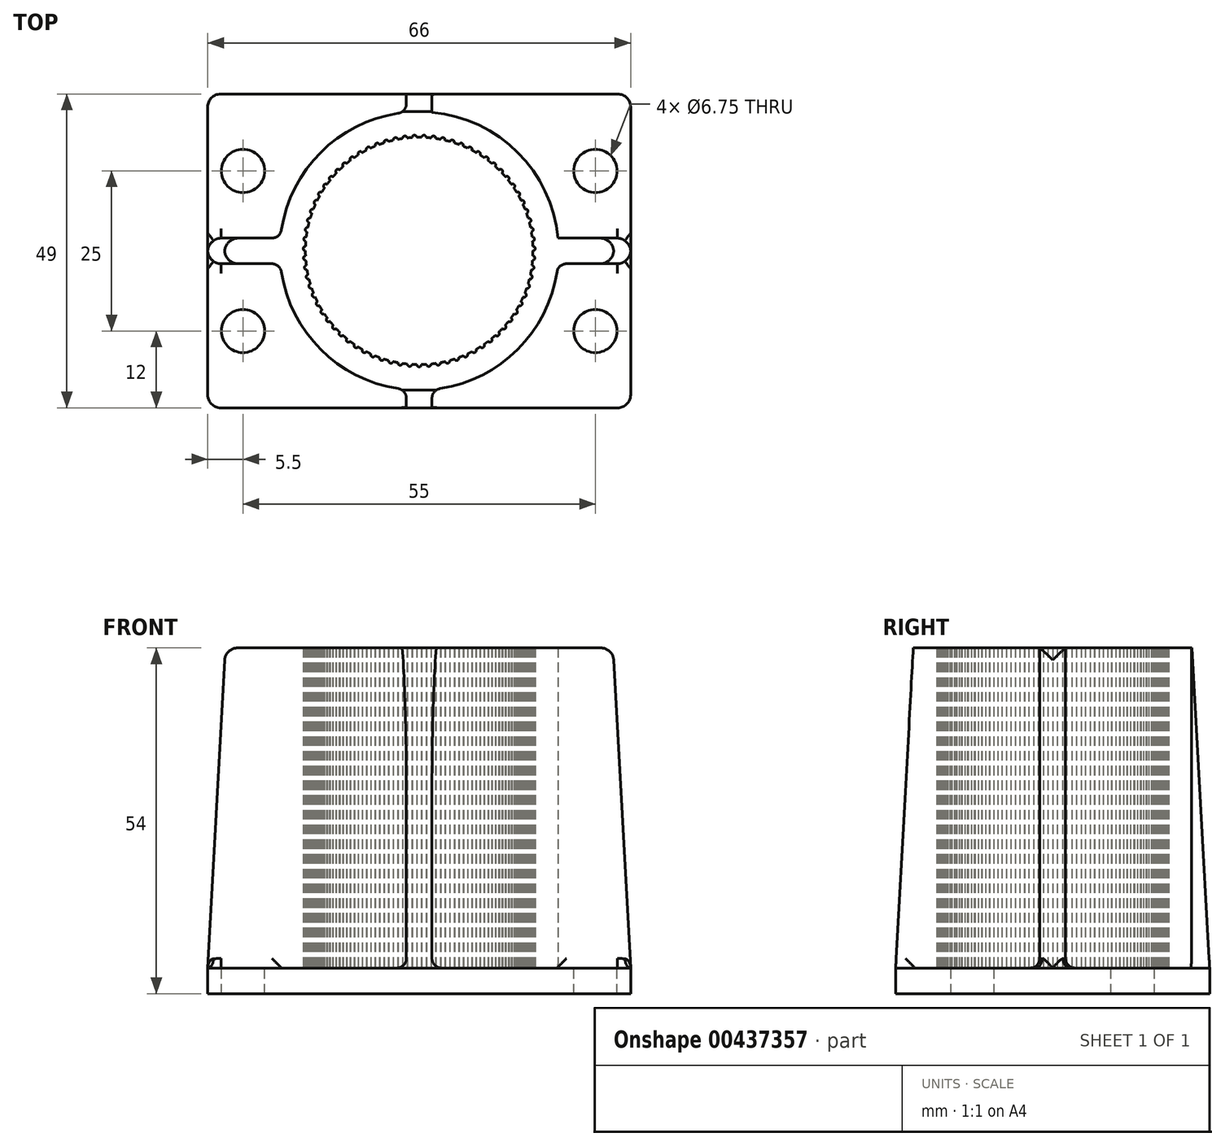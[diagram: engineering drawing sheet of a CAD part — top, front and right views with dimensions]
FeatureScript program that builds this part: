
annotation { "Feature Type Name" : "Feature", "Feature Type Description" : "" }
export const myFeature = defineFeature(function(context is Context, id is Id, definition is map)
    precondition{}
    {
        {
            assignVariable(context, id + "F0", {"name" : "PrintingOffset", "anyValue" : .5});
        }
        {
            assignVariable(context, id + "F1", {"name" : "BoltHoleDiameter", "anyValue" : 6.25 + getVariable(context, 'PrintingOffset')});
        }
        {
            assignVariable(context, id + "F2", {"name" : "PlateWidth", "anyValue" : 49});
        }
        {
            assignVariable(context, id + "F3", {"name" : "TableLegDiameter", "anyValue" : 35 + getVariable(context, 'PrintingOffset')});
        }
        {
            assignVariable(context, id + "F4", {"name" : "WallThickness", "anyValue" : 4});
        }
        {
            var Q0;
            Q0=qCreatedBy(makeId("Top.planeOp"),FACE);
            var sketch = newSketch(context, id + "F5", { "sketchPlane" : qUnion([Q0])});
            skLineSegment(sketch, "E0.rect.bottom", {"start": v(33, 24.5) * mm, "end": v(-33, 24.5) * mm});
            skLineSegment(sketch, "E0.rect.top", {"start": v(33, -24.5) * mm, "end": v(-33, -24.5) * mm});
            skLineSegment(sketch, "E0.rect.left", {"start": v(33, 24.5) * mm, "end": v(33, -24.5) * mm});
            skLineSegment(sketch, "E0.rect.right", {"start": v(-33, 24.5) * mm, "end": v(-33, -24.5) * mm});
            skPoint(sketch, "E0.rect.middle", {"position": v(0, 0) * mm});
            skCircle(sketch, "E1", {"center": v(0, 0) * mm, "radius": 17.75 * mm});
            skLineSegment(sketch, "E2", {"start": v(0, 24.5) * mm, "end": v(0, -24.5) * mm, "construction": true});
            skLineSegment(sketch, "E3", {"start": v(-33, 0) * mm, "end": v(33, 0) * mm, "construction": true});
            skCircle(sketch, "E4.0", {"center": v(0, 0) * mm, "radius": 21.75 * mm});
            skLineSegment(sketch, "E5.3.0", {"start": v(-21.66, 2) * mm, "end": v(-33, 2) * mm});
            skLineSegment(sketch, "E5.3.1", {"start": v(-21.66, -2) * mm, "end": v(-33, -2) * mm});
            skPoint(sketch, "E6", {"position": v(-27.5, 12.5) * mm});
            skArc(sketch, "E7", {"start": v(-0.35, -17.75) * mm, "mid": v(0, -18.1) * mm, "end": v(0.35, -17.75) * mm});
            skArc(sketch, "E8.1.0", {"start": v(1.14, -17.71) * mm, "mid": v(1.51, -18.04) * mm, "end": v(1.83, -17.66) * mm});
            skArc(sketch, "E8.2.0", {"start": v(2.61, -17.56) * mm, "mid": v(3.02, -17.85) * mm, "end": v(3.3, -17.44) * mm});
            skArc(sketch, "E8.3.0", {"start": v(4.07, -17.28) * mm, "mid": v(4.5, -17.53) * mm, "end": v(4.75, -17.1) * mm});
            skArc(sketch, "E8.4.0", {"start": v(5.5, -16.87) * mm, "mid": v(5.95, -17.1) * mm, "end": v(6.17, -16.64) * mm});
            skArc(sketch, "E8.5.0", {"start": v(6.9, -16.35) * mm, "mid": v(7.36, -16.54) * mm, "end": v(7.54, -16.07) * mm});
            skArc(sketch, "E8.6.0", {"start": v(8.24, -15.72) * mm, "mid": v(8.72, -15.86) * mm, "end": v(8.86, -15.38) * mm});
            skArc(sketch, "E8.7.0", {"start": v(9.53, -14.98) * mm, "mid": v(10.02, -15.08) * mm, "end": v(10.11, -14.59) * mm});
            skArc(sketch, "E8.8.0", {"start": v(10.75, -14.13) * mm, "mid": v(11.24, -14.18) * mm, "end": v(11.3, -13.7) * mm});
            skArc(sketch, "E8.9.0", {"start": v(11.9, -13.18) * mm, "mid": v(12.4, -13.2) * mm, "end": v(12.4, -12.7) * mm});
            skArc(sketch, "E8.10.0", {"start": v(12.95, -12.13) * mm, "mid": v(13.45, -12.11) * mm, "end": v(13.42, -11.61) * mm});
            skArc(sketch, "E8.11.0", {"start": v(13.92, -11) * mm, "mid": v(14.42, -10.94) * mm, "end": v(14.35, -10.45) * mm});
            skArc(sketch, "E8.12.0", {"start": v(14.8, -9.8) * mm, "mid": v(15.28, -9.7) * mm, "end": v(15.17, -9.21) * mm});
            skArc(sketch, "E8.13.0", {"start": v(15.56, -8.53) * mm, "mid": v(16.04, -8.39) * mm, "end": v(15.89, -7.91) * mm});
            skArc(sketch, "E8.14.0", {"start": v(16.22, -7.2) * mm, "mid": v(16.69, -7.01) * mm, "end": v(16.5, -6.55) * mm});
            skArc(sketch, "E8.15.0", {"start": v(16.77, -5.82) * mm, "mid": v(17.21, -5.6) * mm, "end": v(16.99, -5.15) * mm});
            skArc(sketch, "E8.16.0", {"start": v(17.2, -4.4) * mm, "mid": v(17.62, -4.13) * mm, "end": v(17.36, -3.71) * mm});
            skArc(sketch, "E8.17.0", {"start": v(17.5, -2.94) * mm, "mid": v(17.9, -2.64) * mm, "end": v(17.6, -2.25) * mm});
            skArc(sketch, "E8.18.0", {"start": v(17.69, -1.46) * mm, "mid": v(18.06, -1.14) * mm, "end": v(17.73, -0.77) * mm});
            skArc(sketch, "E8.19.0", {"start": v(17.75, 0.02) * mm, "mid": v(18.1, 0.38) * mm, "end": v(17.74, 0.72) * mm});
            skArc(sketch, "E8.20.0", {"start": v(17.69, 1.5) * mm, "mid": v(18, 1.9) * mm, "end": v(17.61, 2.2) * mm});
            skArc(sketch, "E8.21.0", {"start": v(17.5, 2.98) * mm, "mid": v(17.78, 3.4) * mm, "end": v(17.37, 3.67) * mm});
            skArc(sketch, "E8.22.0", {"start": v(17.19, 4.44) * mm, "mid": v(17.43, 4.87) * mm, "end": v(17, 5.1) * mm});
            skArc(sketch, "E8.23.0", {"start": v(16.76, 5.86) * mm, "mid": v(16.96, 6.3) * mm, "end": v(16.51, 6.51) * mm});
            skArc(sketch, "E8.24.0", {"start": v(16.2, 7.24) * mm, "mid": v(16.38, 7.7) * mm, "end": v(15.9, 7.87) * mm});
            skArc(sketch, "E8.25.0", {"start": v(15.54, 8.57) * mm, "mid": v(15.68, 9.05) * mm, "end": v(15.2, 9.18) * mm});
            skArc(sketch, "E8.26.0", {"start": v(14.77, 9.84) * mm, "mid": v(14.86, 10.33) * mm, "end": v(14.37, 10.42) * mm});
            skArc(sketch, "E8.27.0", {"start": v(13.9, 11.04) * mm, "mid": v(13.95, 11.54) * mm, "end": v(13.45, 11.58) * mm});
            skArc(sketch, "E8.28.0", {"start": v(12.92, 12.17) * mm, "mid": v(12.93, 12.66) * mm, "end": v(12.43, 12.67) * mm});
            skArc(sketch, "E8.29.0", {"start": v(11.86, 13.2) * mm, "mid": v(11.83, 13.7) * mm, "end": v(11.33, 13.66) * mm});
            skArc(sketch, "E8.30.0", {"start": v(10.71, 14.15) * mm, "mid": v(10.64, 14.64) * mm, "end": v(10.15, 14.56) * mm});
            skArc(sketch, "E8.31.0", {"start": v(9.5, 15) * mm, "mid": v(9.38, 15.48) * mm, "end": v(8.9, 15.36) * mm});
            skArc(sketch, "E8.32.0", {"start": v(8.2, 15.74) * mm, "mid": v(8.05, 16.21) * mm, "end": v(7.58, 16.05) * mm});
            skArc(sketch, "E8.33.0", {"start": v(6.86, 16.37) * mm, "mid": v(6.66, 16.83) * mm, "end": v(6.2, 16.63) * mm});
            skArc(sketch, "E8.34.0", {"start": v(5.46, 16.89) * mm, "mid": v(5.23, 17.33) * mm, "end": v(4.8, 17.1) * mm});
            skArc(sketch, "E8.35.0", {"start": v(4.03, 17.29) * mm, "mid": v(3.76, 17.7) * mm, "end": v(3.35, 17.43) * mm});
            skArc(sketch, "E8.36.0", {"start": v(2.57, 17.56) * mm, "mid": v(2.27, 17.96) * mm, "end": v(1.88, 17.65) * mm});
            skArc(sketch, "E8.37.0", {"start": v(1.1, 17.72) * mm, "mid": v(0.76, 18.08) * mm, "end": v(0.4, 17.75) * mm});
            skArc(sketch, "E8.38.0", {"start": v(-0.4, 17.75) * mm, "mid": v(-0.76, 18.08) * mm, "end": v(-1.1, 17.72) * mm});
            skArc(sketch, "E8.39.0", {"start": v(-1.88, 17.65) * mm, "mid": v(-2.27, 17.96) * mm, "end": v(-2.57, 17.56) * mm});
            skArc(sketch, "E8.40.0", {"start": v(-3.35, 17.43) * mm, "mid": v(-3.76, 17.7) * mm, "end": v(-4.03, 17.29) * mm});
            skArc(sketch, "E8.41.0", {"start": v(-4.8, 17.1) * mm, "mid": v(-5.23, 17.33) * mm, "end": v(-5.46, 16.89) * mm});
            skArc(sketch, "E8.42.0", {"start": v(-6.2, 16.63) * mm, "mid": v(-6.66, 16.83) * mm, "end": v(-6.86, 16.37) * mm});
            skArc(sketch, "E8.43.0", {"start": v(-7.58, 16.05) * mm, "mid": v(-8.05, 16.21) * mm, "end": v(-8.2, 15.74) * mm});
            skArc(sketch, "E8.44.0", {"start": v(-8.9, 15.36) * mm, "mid": v(-9.38, 15.48) * mm, "end": v(-9.5, 15) * mm});
            skArc(sketch, "E8.45.0", {"start": v(-10.15, 14.56) * mm, "mid": v(-10.64, 14.64) * mm, "end": v(-10.71, 14.15) * mm});
            skArc(sketch, "E8.46.0", {"start": v(-11.33, 13.66) * mm, "mid": v(-11.83, 13.7) * mm, "end": v(-11.86, 13.2) * mm});
            skArc(sketch, "E8.47.0", {"start": v(-12.43, 12.67) * mm, "mid": v(-12.93, 12.66) * mm, "end": v(-12.92, 12.17) * mm});
            skArc(sketch, "E8.48.0", {"start": v(-13.45, 11.58) * mm, "mid": v(-13.95, 11.54) * mm, "end": v(-13.9, 11.04) * mm});
            skArc(sketch, "E8.49.0", {"start": v(-14.37, 10.42) * mm, "mid": v(-14.86, 10.33) * mm, "end": v(-14.77, 9.84) * mm});
            skArc(sketch, "E8.50.0", {"start": v(-15.2, 9.18) * mm, "mid": v(-15.68, 9.05) * mm, "end": v(-15.54, 8.57) * mm});
            skArc(sketch, "E8.51.0", {"start": v(-15.9, 7.87) * mm, "mid": v(-16.38, 7.7) * mm, "end": v(-16.2, 7.24) * mm});
            skArc(sketch, "E8.52.0", {"start": v(-16.51, 6.51) * mm, "mid": v(-16.96, 6.3) * mm, "end": v(-16.76, 5.86) * mm});
            skArc(sketch, "E8.53.0", {"start": v(-17, 5.1) * mm, "mid": v(-17.43, 4.87) * mm, "end": v(-17.19, 4.44) * mm});
            skArc(sketch, "E8.54.0", {"start": v(-17.37, 3.67) * mm, "mid": v(-17.78, 3.4) * mm, "end": v(-17.5, 2.98) * mm});
            skArc(sketch, "E8.55.0", {"start": v(-17.61, 2.2) * mm, "mid": v(-18, 1.9) * mm, "end": v(-17.69, 1.5) * mm});
            skArc(sketch, "E8.56.0", {"start": v(-17.74, 0.72) * mm, "mid": v(-18.1, 0.38) * mm, "end": v(-17.75, 0.02) * mm});
            skArc(sketch, "E8.57.0", {"start": v(-17.73, -0.77) * mm, "mid": v(-18.06, -1.14) * mm, "end": v(-17.69, -1.46) * mm});
            skArc(sketch, "E8.58.0", {"start": v(-17.6, -2.25) * mm, "mid": v(-17.9, -2.64) * mm, "end": v(-17.5, -2.94) * mm});
            skArc(sketch, "E8.59.0", {"start": v(-17.36, -3.71) * mm, "mid": v(-17.62, -4.13) * mm, "end": v(-17.2, -4.4) * mm});
            skArc(sketch, "E8.60.0", {"start": v(-16.99, -5.15) * mm, "mid": v(-17.21, -5.6) * mm, "end": v(-16.77, -5.82) * mm});
            skArc(sketch, "E8.61.0", {"start": v(-16.5, -6.55) * mm, "mid": v(-16.69, -7.01) * mm, "end": v(-16.22, -7.2) * mm});
            skArc(sketch, "E8.62.0", {"start": v(-15.89, -7.91) * mm, "mid": v(-16.04, -8.39) * mm, "end": v(-15.56, -8.53) * mm});
            skArc(sketch, "E8.63.0", {"start": v(-15.17, -9.21) * mm, "mid": v(-15.28, -9.7) * mm, "end": v(-14.8, -9.8) * mm});
            skArc(sketch, "E8.64.0", {"start": v(-14.35, -10.45) * mm, "mid": v(-14.42, -10.94) * mm, "end": v(-13.92, -11) * mm});
            skArc(sketch, "E8.65.0", {"start": v(-13.42, -11.61) * mm, "mid": v(-13.45, -12.11) * mm, "end": v(-12.95, -12.13) * mm});
            skArc(sketch, "E8.66.0", {"start": v(-12.4, -12.7) * mm, "mid": v(-12.4, -13.2) * mm, "end": v(-11.9, -13.18) * mm});
            skArc(sketch, "E8.67.0", {"start": v(-11.3, -13.7) * mm, "mid": v(-11.24, -14.18) * mm, "end": v(-10.75, -14.13) * mm});
            skArc(sketch, "E8.68.0", {"start": v(-10.11, -14.59) * mm, "mid": v(-10.02, -15.08) * mm, "end": v(-9.53, -14.98) * mm});
            skArc(sketch, "E8.69.0", {"start": v(-8.86, -15.38) * mm, "mid": v(-8.72, -15.86) * mm, "end": v(-8.24, -15.72) * mm});
            skArc(sketch, "E9.2.70.0", {"start": v(-7.54, -16.07) * mm, "mid": v(-7.36, -16.54) * mm, "end": v(-6.9, -16.35) * mm});
            skArc(sketch, "E9.2.71.0", {"start": v(-6.17, -16.64) * mm, "mid": v(-5.95, -17.1) * mm, "end": v(-5.5, -16.87) * mm});
            skArc(sketch, "E9.2.72.0", {"start": v(-4.75, -17.1) * mm, "mid": v(-4.5, -17.53) * mm, "end": v(-4.07, -17.28) * mm});
            skArc(sketch, "E9.2.73.0", {"start": v(-3.3, -17.44) * mm, "mid": v(-3.02, -17.85) * mm, "end": v(-2.61, -17.56) * mm});
            skArc(sketch, "E9.2.74.0", {"start": v(-1.83, -17.66) * mm, "mid": v(-1.51, -18.04) * mm, "end": v(-1.14, -17.71) * mm});
            skLineSegment(sketch, "E10.MirrorCS", {"start": v(21.66, -2) * mm, "end": v(33, -2) * mm});
            skLineSegment(sketch, "E11.MirrorCS", {"start": v(21.66, 2) * mm, "end": v(33, 2) * mm});
            skLineSegment(sketch, "E12.MirrorCS", {"start": v(-2, 21.66) * mm, "end": v(-2, 24.5) * mm});
            skLineSegment(sketch, "E13.MirrorCS", {"start": v(2, 21.66) * mm, "end": v(2, 24.5) * mm});
            skLineSegment(sketch, "E14.MirrorCS", {"start": v(-2, -21.66) * mm, "end": v(-2, -24.5) * mm});
            skLineSegment(sketch, "E15.MirrorCS", {"start": v(2, -21.66) * mm, "end": v(2, -24.5) * mm});
            skPoint(sketch, "E16.MirrorP", {"position": v(-27.5, -12.5) * mm});
            skPoint(sketch, "E17.MirrorP", {"position": v(27.5, 12.5) * mm});
            skPoint(sketch, "E18.MirrorP", {"position": v(27.5, -12.5) * mm});
            skSolve(sketch);
        }
        {
            assignVariable(context, id + "F6", {"name" : "CylinderHeight", "anyValue" : 50});
        }
        {
            var Q0;
            Q0=makeQuery(id+"F5.imprint","IMPRINT",FACE,{"disambiguationData":[TD([[makeQuery(id+"F5.imprint","IMPRINT",EDGE,{"derivedFrom":sQuery(id+"F5.wireOp",EDGE,"E1")}),-1.0]])]});
            extrude(context, id + "F7", {"entities" : qUnion([Q0]), "depth" : (getVariable(context, 'CylinderHeight')) * mm});
        }
        {
            var Q0;
            {var subQ1=sQuery(id+"F5.wireOp",EDGE,"E5.3.0");Q0=makeQuery(id+"F5.imprint","IMPRINT",FACE,{"disambiguationData":[TD([[makeQuery(id+"F5.imprint","IMPRINT",EDGE,{"derivedFrom":subQ1}),1.0]])]});}
            var Q1;
            {var subQ2=sQuery(id+"F5.wireOp",EDGE,"E5.1.1");Q1=makeQuery(id+"F5.imprint","IMPRINT",FACE,{"disambiguationData":[TD([[makeQuery(id+"F5.imprint","IMPRINT",EDGE,{"derivedFrom":subQ2}),1.0]])]});}
            var Q2;
            {var subQ0=sQuery(id+"F5.wireOp",EDGE,"E1");var subQ1=sQuery(id+"F5.wireOp",EDGE,"E8.25.0");var subQ174=makeQuery(id+"F5.imprint","INTERSECT",VERTEX,{"disambiguationData":[OD(1.0)],"derivedFrom":[subQ0,subQ1]});Q2=makeQuery(id+"F5.imprint","IMPRINT",FACE,{"disambiguationData":[TD([[makeQuery(id+"F5.imprint","IMPRINT",EDGE,{"disambiguationData":[TD([[subQ174,-1.0]])],"derivedFrom":subQ0}),1.0]])]});}
            var Q3;
            {var subQ0=sQuery(id+"F5.wireOp",EDGE,"E5.1.0");Q3=makeQuery(id+"F5.imprint","IMPRINT",FACE,{"disambiguationData":[TD([[makeQuery(id+"F5.imprint","IMPRINT",EDGE,{"derivedFrom":subQ0}),1.0]])]});}
            var Q4;
            {var subQ86=sQuery(id+"F5.wireOp",EDGE,"E7");Q4=makeQuery(id+"F5.imprint","IMPRINT",FACE,{"disambiguationData":[TD([[makeQuery(id+"F5.imprint","IMPRINT",EDGE,{"derivedFrom":subQ86}),-1.0]])]});}
            var Q5;
            {var subQ1=sQuery(id+"F5.wireOp",EDGE,"E5.2.0");Q5=makeQuery(id+"F5.imprint","IMPRINT",FACE,{"disambiguationData":[TD([[makeQuery(id+"F5.imprint","IMPRINT",EDGE,{"derivedFrom":subQ1}),1.0]])]});}
            var Q6;
            {var subQ1=sQuery(id+"F5.wireOp",EDGE,"E5.2.1");Q6=makeQuery(id+"F5.imprint","IMPRINT",FACE,{"disambiguationData":[TD([[makeQuery(id+"F5.imprint","IMPRINT",EDGE,{"derivedFrom":subQ1}),1.0]])]});}
            var Q7;
            {var subQ0=sQuery(id+"F5.wireOp",EDGE,"108301c5-a481-47a9-95d8-fa25c03050fa");Q7=makeQuery(id+"F5.imprint","IMPRINT",FACE,{"disambiguationData":[TD([[makeQuery(id+"F5.imprint","IMPRINT",EDGE,{"derivedFrom":subQ0}),1.0]])]});}
            var Q8;
            {var subQ1=sQuery(id+"F5.wireOp",EDGE,"79e71fa4-d721-44c3-a3e5-dd1a67dfb6ba");Q8=makeQuery(id+"F5.imprint","IMPRINT",FACE,{"disambiguationData":[TD([[makeQuery(id+"F5.imprint","IMPRINT",EDGE,{"derivedFrom":subQ1}),1.0]])]});}
            var Q9;
            {var subQ1=sQuery(id+"F5.wireOp",EDGE,"79e71fa4-d721-44c3-a3e5-dd1a67dfb6ba");Q9=makeQuery(id+"F5.imprint","IMPRINT",FACE,{"disambiguationData":[TD([[makeQuery(id+"F5.imprint","IMPRINT",EDGE,{"derivedFrom":subQ1}),-1.0]])]});}
            var Q10;
            Q10=makeQuery(id+"F7.opExtrude","CAP_FACE",FACE,{"disambiguationData":[OSD([sQuery(id+"F5.wireOp",EDGE,"E1"),sQuery(id+"F5.wireOp",EDGE,"E4.0"),sQuery(id+"F5.wireOp",EDGE,"E7"),sQuery(id+"F5.wireOp",EDGE,"E8.1.0"),sQuery(id+"F5.wireOp",EDGE,"E8.2.0"),sQuery(id+"F5.wireOp",EDGE,"E8.3.0"),sQuery(id+"F5.wireOp",EDGE,"E8.4.0"),sQuery(id+"F5.wireOp",EDGE,"E8.5.0"),sQuery(id+"F5.wireOp",EDGE,"E8.6.0"),sQuery(id+"F5.wireOp",EDGE,"E8.7.0"),sQuery(id+"F5.wireOp",EDGE,"E8.8.0"),sQuery(id+"F5.wireOp",EDGE,"E8.9.0"),sQuery(id+"F5.wireOp",EDGE,"E8.10.0"),sQuery(id+"F5.wireOp",EDGE,"E8.11.0"),sQuery(id+"F5.wireOp",EDGE,"E8.12.0"),sQuery(id+"F5.wireOp",EDGE,"E8.13.0"),sQuery(id+"F5.wireOp",EDGE,"E8.14.0"),sQuery(id+"F5.wireOp",EDGE,"E8.15.0"),sQuery(id+"F5.wireOp",EDGE,"E8.16.0"),sQuery(id+"F5.wireOp",EDGE,"E8.17.0"),sQuery(id+"F5.wireOp",EDGE,"E8.18.0"),sQuery(id+"F5.wireOp",EDGE,"E8.19.0"),sQuery(id+"F5.wireOp",EDGE,"E8.20.0"),sQuery(id+"F5.wireOp",EDGE,"E8.21.0"),sQuery(id+"F5.wireOp",EDGE,"E8.22.0"),sQuery(id+"F5.wireOp",EDGE,"E8.23.0"),sQuery(id+"F5.wireOp",EDGE,"E8.24.0"),sQuery(id+"F5.wireOp",EDGE,"E8.25.0"),sQuery(id+"F5.wireOp",EDGE,"E8.26.0"),sQuery(id+"F5.wireOp",EDGE,"E8.27.0"),sQuery(id+"F5.wireOp",EDGE,"E8.28.0"),sQuery(id+"F5.wireOp",EDGE,"E8.29.0"),sQuery(id+"F5.wireOp",EDGE,"E8.30.0"),sQuery(id+"F5.wireOp",EDGE,"E8.31.0"),sQuery(id+"F5.wireOp",EDGE,"E8.32.0"),sQuery(id+"F5.wireOp",EDGE,"E8.33.0"),sQuery(id+"F5.wireOp",EDGE,"E8.34.0"),sQuery(id+"F5.wireOp",EDGE,"E8.35.0"),sQuery(id+"F5.wireOp",EDGE,"E8.36.0"),sQuery(id+"F5.wireOp",EDGE,"E8.37.0"),sQuery(id+"F5.wireOp",EDGE,"E8.38.0"),sQuery(id+"F5.wireOp",EDGE,"E8.39.0"),sQuery(id+"F5.wireOp",EDGE,"E8.40.0"),sQuery(id+"F5.wireOp",EDGE,"E8.41.0"),sQuery(id+"F5.wireOp",EDGE,"E8.42.0"),sQuery(id+"F5.wireOp",EDGE,"E8.43.0"),sQuery(id+"F5.wireOp",EDGE,"E8.44.0"),sQuery(id+"F5.wireOp",EDGE,"E8.45.0"),sQuery(id+"F5.wireOp",EDGE,"E8.46.0"),sQuery(id+"F5.wireOp",EDGE,"E8.47.0"),sQuery(id+"F5.wireOp",EDGE,"E8.48.0"),sQuery(id+"F5.wireOp",EDGE,"E8.49.0"),sQuery(id+"F5.wireOp",EDGE,"E8.50.0"),sQuery(id+"F5.wireOp",EDGE,"E8.51.0"),sQuery(id+"F5.wireOp",EDGE,"E8.52.0"),sQuery(id+"F5.wireOp",EDGE,"E8.53.0"),sQuery(id+"F5.wireOp",EDGE,"E8.54.0"),sQuery(id+"F5.wireOp",EDGE,"E8.55.0"),sQuery(id+"F5.wireOp",EDGE,"E8.56.0"),sQuery(id+"F5.wireOp",EDGE,"E8.57.0"),sQuery(id+"F5.wireOp",EDGE,"E8.58.0"),sQuery(id+"F5.wireOp",EDGE,"E8.59.0"),sQuery(id+"F5.wireOp",EDGE,"E8.60.0"),sQuery(id+"F5.wireOp",EDGE,"E8.61.0"),sQuery(id+"F5.wireOp",EDGE,"E8.62.0"),sQuery(id+"F5.wireOp",EDGE,"E8.63.0"),sQuery(id+"F5.wireOp",EDGE,"E8.64.0"),sQuery(id+"F5.wireOp",EDGE,"E8.65.0"),sQuery(id+"F5.wireOp",EDGE,"E8.66.0"),sQuery(id+"F5.wireOp",EDGE,"E8.67.0"),sQuery(id+"F5.wireOp",EDGE,"E8.68.0"),sQuery(id+"F5.wireOp",EDGE,"E8.69.0"),sQuery(id+"F5.wireOp",EDGE,"E8.70.0"),sQuery(id+"F5.wireOp",EDGE,"E8.71.0"),sQuery(id+"F5.wireOp",EDGE,"E8.72.0"),sQuery(id+"F5.wireOp",EDGE,"E8.73.0"),sQuery(id+"F5.wireOp",EDGE,"E8.74.0"),sQuery(id+"F5.wireOp",EDGE,"E8.75.0"),sQuery(id+"F5.wireOp",EDGE,"E8.76.0"),sQuery(id+"F5.wireOp",EDGE,"E8.77.0"),sQuery(id+"F5.wireOp",EDGE,"E8.78.0"),sQuery(id+"F5.wireOp",EDGE,"E8.79.0"),sQuery(id+"F5.wireOp",EDGE,"E8.80.0"),sQuery(id+"F5.wireOp",EDGE,"E8.81.0"),sQuery(id+"F5.wireOp",EDGE,"E8.82.0"),sQuery(id+"F5.wireOp",EDGE,"E8.83.0"),sQuery(id+"F5.wireOp",EDGE,"E8.84.0"),sQuery(id+"F5.wireOp",EDGE,"E8.85.0"),sQuery(id+"F5.wireOp",EDGE,"E8.86.0"),sQuery(id+"F5.wireOp",EDGE,"E8.87.0"),sQuery(id+"F5.wireOp",EDGE,"E8.88.0"),sQuery(id+"F5.wireOp",EDGE,"E8.89.0"),sQuery(id+"F5.wireOp",EDGE,"E8.90.0"),sQuery(id+"F5.wireOp",EDGE,"E8.91.0"),sQuery(id+"F5.wireOp",EDGE,"E8.92.0"),sQuery(id+"F5.wireOp",EDGE,"E8.93.0"),sQuery(id+"F5.wireOp",EDGE,"E8.94.0"),sQuery(id+"F5.wireOp",EDGE,"E8.95.0"),sQuery(id+"F5.wireOp",EDGE,"E8.96.0"),sQuery(id+"F5.wireOp",EDGE,"E8.97.0"),sQuery(id+"F5.wireOp",EDGE,"E8.98.0"),sQuery(id+"F5.wireOp",EDGE,"E8.99.0")])],"isStart":true});
            var Q11;
            Q11=makeQuery(id+"F7.opExtrude","CAP_FACE",FACE,{"disambiguationData":[OSD([sQuery(id+"F5.wireOp",EDGE,"E1"),sQuery(id+"F5.wireOp",EDGE,"E4.0"),sQuery(id+"F5.wireOp",EDGE,"E7"),sQuery(id+"F5.wireOp",EDGE,"E8.1.0"),sQuery(id+"F5.wireOp",EDGE,"E8.2.0"),sQuery(id+"F5.wireOp",EDGE,"E8.3.0"),sQuery(id+"F5.wireOp",EDGE,"E8.4.0"),sQuery(id+"F5.wireOp",EDGE,"E8.5.0"),sQuery(id+"F5.wireOp",EDGE,"E8.6.0"),sQuery(id+"F5.wireOp",EDGE,"E8.7.0"),sQuery(id+"F5.wireOp",EDGE,"E8.8.0"),sQuery(id+"F5.wireOp",EDGE,"E8.9.0"),sQuery(id+"F5.wireOp",EDGE,"E8.10.0"),sQuery(id+"F5.wireOp",EDGE,"E8.11.0"),sQuery(id+"F5.wireOp",EDGE,"E8.12.0"),sQuery(id+"F5.wireOp",EDGE,"E8.13.0"),sQuery(id+"F5.wireOp",EDGE,"E8.14.0"),sQuery(id+"F5.wireOp",EDGE,"E8.15.0"),sQuery(id+"F5.wireOp",EDGE,"E8.16.0"),sQuery(id+"F5.wireOp",EDGE,"E8.17.0"),sQuery(id+"F5.wireOp",EDGE,"E8.18.0"),sQuery(id+"F5.wireOp",EDGE,"E8.19.0"),sQuery(id+"F5.wireOp",EDGE,"E8.20.0"),sQuery(id+"F5.wireOp",EDGE,"E8.21.0"),sQuery(id+"F5.wireOp",EDGE,"E8.22.0"),sQuery(id+"F5.wireOp",EDGE,"E8.23.0"),sQuery(id+"F5.wireOp",EDGE,"E8.24.0"),sQuery(id+"F5.wireOp",EDGE,"E8.25.0"),sQuery(id+"F5.wireOp",EDGE,"E8.26.0"),sQuery(id+"F5.wireOp",EDGE,"E8.27.0"),sQuery(id+"F5.wireOp",EDGE,"E8.28.0"),sQuery(id+"F5.wireOp",EDGE,"E8.29.0"),sQuery(id+"F5.wireOp",EDGE,"E8.30.0"),sQuery(id+"F5.wireOp",EDGE,"E8.31.0"),sQuery(id+"F5.wireOp",EDGE,"E8.32.0"),sQuery(id+"F5.wireOp",EDGE,"E8.33.0"),sQuery(id+"F5.wireOp",EDGE,"E8.34.0"),sQuery(id+"F5.wireOp",EDGE,"E8.35.0"),sQuery(id+"F5.wireOp",EDGE,"E8.36.0"),sQuery(id+"F5.wireOp",EDGE,"E8.37.0"),sQuery(id+"F5.wireOp",EDGE,"E8.38.0"),sQuery(id+"F5.wireOp",EDGE,"E8.39.0"),sQuery(id+"F5.wireOp",EDGE,"E8.40.0"),sQuery(id+"F5.wireOp",EDGE,"E8.41.0"),sQuery(id+"F5.wireOp",EDGE,"E8.42.0"),sQuery(id+"F5.wireOp",EDGE,"E8.43.0"),sQuery(id+"F5.wireOp",EDGE,"E8.44.0"),sQuery(id+"F5.wireOp",EDGE,"E8.45.0"),sQuery(id+"F5.wireOp",EDGE,"E8.46.0"),sQuery(id+"F5.wireOp",EDGE,"E8.47.0"),sQuery(id+"F5.wireOp",EDGE,"E8.48.0"),sQuery(id+"F5.wireOp",EDGE,"E8.49.0"),sQuery(id+"F5.wireOp",EDGE,"E8.50.0"),sQuery(id+"F5.wireOp",EDGE,"E8.51.0"),sQuery(id+"F5.wireOp",EDGE,"E8.52.0"),sQuery(id+"F5.wireOp",EDGE,"E8.53.0"),sQuery(id+"F5.wireOp",EDGE,"E8.54.0"),sQuery(id+"F5.wireOp",EDGE,"E8.55.0"),sQuery(id+"F5.wireOp",EDGE,"E8.56.0"),sQuery(id+"F5.wireOp",EDGE,"E8.57.0"),sQuery(id+"F5.wireOp",EDGE,"E8.58.0"),sQuery(id+"F5.wireOp",EDGE,"E8.59.0"),sQuery(id+"F5.wireOp",EDGE,"E8.60.0"),sQuery(id+"F5.wireOp",EDGE,"E8.61.0"),sQuery(id+"F5.wireOp",EDGE,"E8.62.0"),sQuery(id+"F5.wireOp",EDGE,"E8.63.0"),sQuery(id+"F5.wireOp",EDGE,"E8.64.0"),sQuery(id+"F5.wireOp",EDGE,"E8.65.0"),sQuery(id+"F5.wireOp",EDGE,"E8.66.0"),sQuery(id+"F5.wireOp",EDGE,"E8.67.0"),sQuery(id+"F5.wireOp",EDGE,"E8.68.0"),sQuery(id+"F5.wireOp",EDGE,"E8.69.0"),sQuery(id+"F5.wireOp",EDGE,"E8.70.0"),sQuery(id+"F5.wireOp",EDGE,"E8.71.0"),sQuery(id+"F5.wireOp",EDGE,"E8.72.0"),sQuery(id+"F5.wireOp",EDGE,"E8.73.0"),sQuery(id+"F5.wireOp",EDGE,"E8.74.0"),sQuery(id+"F5.wireOp",EDGE,"E8.75.0"),sQuery(id+"F5.wireOp",EDGE,"E8.76.0"),sQuery(id+"F5.wireOp",EDGE,"E8.77.0"),sQuery(id+"F5.wireOp",EDGE,"E8.78.0"),sQuery(id+"F5.wireOp",EDGE,"E8.79.0"),sQuery(id+"F5.wireOp",EDGE,"E8.80.0"),sQuery(id+"F5.wireOp",EDGE,"E8.81.0"),sQuery(id+"F5.wireOp",EDGE,"E8.82.0"),sQuery(id+"F5.wireOp",EDGE,"E8.83.0"),sQuery(id+"F5.wireOp",EDGE,"E8.84.0"),sQuery(id+"F5.wireOp",EDGE,"E8.85.0"),sQuery(id+"F5.wireOp",EDGE,"E8.86.0"),sQuery(id+"F5.wireOp",EDGE,"E8.87.0"),sQuery(id+"F5.wireOp",EDGE,"E8.88.0"),sQuery(id+"F5.wireOp",EDGE,"E8.89.0"),sQuery(id+"F5.wireOp",EDGE,"E8.90.0"),sQuery(id+"F5.wireOp",EDGE,"E8.91.0"),sQuery(id+"F5.wireOp",EDGE,"E8.92.0"),sQuery(id+"F5.wireOp",EDGE,"E8.93.0"),sQuery(id+"F5.wireOp",EDGE,"E8.94.0"),sQuery(id+"F5.wireOp",EDGE,"E8.95.0"),sQuery(id+"F5.wireOp",EDGE,"E8.96.0"),sQuery(id+"F5.wireOp",EDGE,"E8.97.0"),sQuery(id+"F5.wireOp",EDGE,"E8.98.0"),sQuery(id+"F5.wireOp",EDGE,"E8.99.0")])],"isStart":false});
            var Q12;
            {var subQ0=sQuery(id+"F5.wireOp",EDGE,"E8.86.0");Q12=makeQuery(id+"F5.imprint","IMPRINT",FACE,{"disambiguationData":[TD([[makeQuery(id+"F5.imprint","IMPRINT",EDGE,{"derivedFrom":subQ0}),1.0]])]});}
            var Q13;
            {var subQ0=sQuery(id+"F5.wireOp",EDGE,"E8.79.0");Q13=makeQuery(id+"F5.imprint","IMPRINT",FACE,{"disambiguationData":[TD([[makeQuery(id+"F5.imprint","IMPRINT",EDGE,{"derivedFrom":subQ0}),1.0]])]});}
            var Q14;
            {var subQ0=sQuery(id+"F5.wireOp",EDGE,"E8.31.0");Q14=makeQuery(id+"F5.imprint","IMPRINT",FACE,{"disambiguationData":[TD([[makeQuery(id+"F5.imprint","IMPRINT",EDGE,{"derivedFrom":subQ0}),1.0]])]});}
            var Q15;
            {var subQ0=sQuery(id+"F5.wireOp",EDGE,"E8.32.0");Q15=makeQuery(id+"F5.imprint","IMPRINT",FACE,{"disambiguationData":[TD([[makeQuery(id+"F5.imprint","IMPRINT",EDGE,{"derivedFrom":subQ0}),1.0]])]});}
            var Q16;
            {var subQ0=sQuery(id+"F5.wireOp",EDGE,"E8.21.0");Q16=makeQuery(id+"F5.imprint","IMPRINT",FACE,{"disambiguationData":[TD([[makeQuery(id+"F5.imprint","IMPRINT",EDGE,{"derivedFrom":subQ0}),1.0]])]});}
            var Q17;
            {var subQ0=sQuery(id+"F5.wireOp",EDGE,"E8.71.0");Q17=makeQuery(id+"F5.imprint","IMPRINT",FACE,{"disambiguationData":[TD([[makeQuery(id+"F5.imprint","IMPRINT",EDGE,{"derivedFrom":subQ0}),1.0]])]});}
            var Q18;
            {var subQ0=sQuery(id+"F5.wireOp",EDGE,"E8.78.0");Q18=makeQuery(id+"F5.imprint","IMPRINT",FACE,{"disambiguationData":[TD([[makeQuery(id+"F5.imprint","IMPRINT",EDGE,{"derivedFrom":subQ0}),1.0]])]});}
            var Q19;
            {var subQ0=sQuery(id+"F5.wireOp",EDGE,"E8.25.0");Q19=makeQuery(id+"F5.imprint","IMPRINT",FACE,{"disambiguationData":[TD([[makeQuery(id+"F5.imprint","IMPRINT",EDGE,{"derivedFrom":subQ0}),1.0]])]});}
            var Q20;
            {var subQ0=sQuery(id+"F5.wireOp",EDGE,"E8.61.0");Q20=makeQuery(id+"F5.imprint","IMPRINT",FACE,{"disambiguationData":[TD([[makeQuery(id+"F5.imprint","IMPRINT",EDGE,{"derivedFrom":subQ0}),1.0]])]});}
            var Q21;
            {var subQ0=sQuery(id+"F5.wireOp",EDGE,"E8.45.0");Q21=makeQuery(id+"F5.imprint","IMPRINT",FACE,{"disambiguationData":[TD([[makeQuery(id+"F5.imprint","IMPRINT",EDGE,{"derivedFrom":subQ0}),1.0]])]});}
            var Q22;
            {var subQ0=sQuery(id+"F5.wireOp",EDGE,"E8.10.0");Q22=makeQuery(id+"F5.imprint","IMPRINT",FACE,{"disambiguationData":[TD([[makeQuery(id+"F5.imprint","IMPRINT",EDGE,{"derivedFrom":subQ0}),1.0]])]});}
            var Q23;
            {var subQ0=sQuery(id+"F5.wireOp",EDGE,"E8.7.0");Q23=makeQuery(id+"F5.imprint","IMPRINT",FACE,{"disambiguationData":[TD([[makeQuery(id+"F5.imprint","IMPRINT",EDGE,{"derivedFrom":subQ0}),1.0]])]});}
            var Q24;
            {var subQ0=sQuery(id+"F5.wireOp",EDGE,"E8.43.0");Q24=makeQuery(id+"F5.imprint","IMPRINT",FACE,{"disambiguationData":[TD([[makeQuery(id+"F5.imprint","IMPRINT",EDGE,{"derivedFrom":subQ0}),1.0]])]});}
            var Q25;
            {var subQ0=sQuery(id+"F5.wireOp",EDGE,"E8.22.0");Q25=makeQuery(id+"F5.imprint","IMPRINT",FACE,{"disambiguationData":[TD([[makeQuery(id+"F5.imprint","IMPRINT",EDGE,{"derivedFrom":subQ0}),1.0]])]});}
            var Q26;
            {var subQ0=sQuery(id+"F5.wireOp",EDGE,"E8.90.0");Q26=makeQuery(id+"F5.imprint","IMPRINT",FACE,{"disambiguationData":[TD([[makeQuery(id+"F5.imprint","IMPRINT",EDGE,{"derivedFrom":subQ0}),1.0]])]});}
            var Q27;
            {var subQ0=sQuery(id+"F5.wireOp",EDGE,"E8.58.0");Q27=makeQuery(id+"F5.imprint","IMPRINT",FACE,{"disambiguationData":[TD([[makeQuery(id+"F5.imprint","IMPRINT",EDGE,{"derivedFrom":subQ0}),1.0]])]});}
            var Q28;
            {var subQ0=sQuery(id+"F5.wireOp",EDGE,"E8.70.0");Q28=makeQuery(id+"F5.imprint","IMPRINT",FACE,{"disambiguationData":[TD([[makeQuery(id+"F5.imprint","IMPRINT",EDGE,{"derivedFrom":subQ0}),1.0]])]});}
            var Q29;
            {var subQ0=sQuery(id+"F5.wireOp",EDGE,"E8.20.0");Q29=makeQuery(id+"F5.imprint","IMPRINT",FACE,{"disambiguationData":[TD([[makeQuery(id+"F5.imprint","IMPRINT",EDGE,{"derivedFrom":subQ0}),1.0]])]});}
            var Q30;
            {var subQ0=sQuery(id+"F5.wireOp",EDGE,"E8.72.0");Q30=makeQuery(id+"F5.imprint","IMPRINT",FACE,{"disambiguationData":[TD([[makeQuery(id+"F5.imprint","IMPRINT",EDGE,{"derivedFrom":subQ0}),1.0]])]});}
            var Q31;
            {var subQ0=sQuery(id+"F5.wireOp",EDGE,"E8.88.0");Q31=makeQuery(id+"F5.imprint","IMPRINT",FACE,{"disambiguationData":[TD([[makeQuery(id+"F5.imprint","IMPRINT",EDGE,{"derivedFrom":subQ0}),1.0]])]});}
            var Q32;
            {var subQ0=sQuery(id+"F5.wireOp",EDGE,"E8.17.0");Q32=makeQuery(id+"F5.imprint","IMPRINT",FACE,{"disambiguationData":[TD([[makeQuery(id+"F5.imprint","IMPRINT",EDGE,{"derivedFrom":subQ0}),1.0]])]});}
            var Q33;
            {var subQ0=sQuery(id+"F5.wireOp",EDGE,"E8.69.0");Q33=makeQuery(id+"F5.imprint","IMPRINT",FACE,{"disambiguationData":[TD([[makeQuery(id+"F5.imprint","IMPRINT",EDGE,{"derivedFrom":subQ0}),1.0]])]});}
            var Q34;
            {var subQ0=sQuery(id+"F5.wireOp",EDGE,"E8.19.0");Q34=makeQuery(id+"F5.imprint","IMPRINT",FACE,{"disambiguationData":[TD([[makeQuery(id+"F5.imprint","IMPRINT",EDGE,{"derivedFrom":subQ0}),1.0]])]});}
            var Q35;
            {var subQ0=sQuery(id+"F5.wireOp",EDGE,"E8.85.0");Q35=makeQuery(id+"F5.imprint","IMPRINT",FACE,{"disambiguationData":[TD([[makeQuery(id+"F5.imprint","IMPRINT",EDGE,{"derivedFrom":subQ0}),1.0]])]});}
            var Q36;
            {var subQ0=sQuery(id+"F5.wireOp",EDGE,"E8.24.0");Q36=makeQuery(id+"F5.imprint","IMPRINT",FACE,{"disambiguationData":[TD([[makeQuery(id+"F5.imprint","IMPRINT",EDGE,{"derivedFrom":subQ0}),1.0]])]});}
            var Q37;
            {var subQ0=sQuery(id+"F5.wireOp",EDGE,"E8.23.0");Q37=makeQuery(id+"F5.imprint","IMPRINT",FACE,{"disambiguationData":[TD([[makeQuery(id+"F5.imprint","IMPRINT",EDGE,{"derivedFrom":subQ0}),1.0]])]});}
            var Q38;
            {var subQ0=sQuery(id+"F5.wireOp",EDGE,"E8.56.0");Q38=makeQuery(id+"F5.imprint","IMPRINT",FACE,{"disambiguationData":[TD([[makeQuery(id+"F5.imprint","IMPRINT",EDGE,{"derivedFrom":subQ0}),1.0]])]});}
            var Q39;
            {var subQ0=sQuery(id+"F5.wireOp",EDGE,"E8.95.0");Q39=makeQuery(id+"F5.imprint","IMPRINT",FACE,{"disambiguationData":[TD([[makeQuery(id+"F5.imprint","IMPRINT",EDGE,{"derivedFrom":subQ0}),1.0]])]});}
            var Q40;
            {var subQ0=sQuery(id+"F5.wireOp",EDGE,"E8.47.0");Q40=makeQuery(id+"F5.imprint","IMPRINT",FACE,{"disambiguationData":[TD([[makeQuery(id+"F5.imprint","IMPRINT",EDGE,{"derivedFrom":subQ0}),1.0]])]});}
            var Q41;
            {var subQ0=sQuery(id+"F5.wireOp",EDGE,"E8.12.0");Q41=makeQuery(id+"F5.imprint","IMPRINT",FACE,{"disambiguationData":[TD([[makeQuery(id+"F5.imprint","IMPRINT",EDGE,{"derivedFrom":subQ0}),1.0]])]});}
            var Q42;
            {var subQ0=sQuery(id+"F5.wireOp",EDGE,"E8.96.0");Q42=makeQuery(id+"F5.imprint","IMPRINT",FACE,{"disambiguationData":[TD([[makeQuery(id+"F5.imprint","IMPRINT",EDGE,{"derivedFrom":subQ0}),1.0]])]});}
            var Q43;
            {var subQ0=sQuery(id+"F5.wireOp",EDGE,"E8.48.0");Q43=makeQuery(id+"F5.imprint","IMPRINT",FACE,{"disambiguationData":[TD([[makeQuery(id+"F5.imprint","IMPRINT",EDGE,{"derivedFrom":subQ0}),1.0]])]});}
            var Q44;
            {var subQ0=sQuery(id+"F5.wireOp",EDGE,"E8.26.0");Q44=makeQuery(id+"F5.imprint","IMPRINT",FACE,{"disambiguationData":[TD([[makeQuery(id+"F5.imprint","IMPRINT",EDGE,{"derivedFrom":subQ0}),1.0]])]});}
            var Q45;
            {var subQ0=sQuery(id+"F5.wireOp",EDGE,"E8.27.0");Q45=makeQuery(id+"F5.imprint","IMPRINT",FACE,{"disambiguationData":[TD([[makeQuery(id+"F5.imprint","IMPRINT",EDGE,{"derivedFrom":subQ0}),1.0]])]});}
            var Q46;
            {var subQ0=sQuery(id+"F5.wireOp",EDGE,"E8.28.0");Q46=makeQuery(id+"F5.imprint","IMPRINT",FACE,{"disambiguationData":[TD([[makeQuery(id+"F5.imprint","IMPRINT",EDGE,{"derivedFrom":subQ0}),1.0]])]});}
            var Q47;
            {var subQ0=sQuery(id+"F5.wireOp",EDGE,"E8.29.0");Q47=makeQuery(id+"F5.imprint","IMPRINT",FACE,{"disambiguationData":[TD([[makeQuery(id+"F5.imprint","IMPRINT",EDGE,{"derivedFrom":subQ0}),1.0]])]});}
            var Q48;
            {var subQ0=sQuery(id+"F5.wireOp",EDGE,"E8.33.0");Q48=makeQuery(id+"F5.imprint","IMPRINT",FACE,{"disambiguationData":[TD([[makeQuery(id+"F5.imprint","IMPRINT",EDGE,{"derivedFrom":subQ0}),1.0]])]});}
            var Q49;
            {var subQ0=sQuery(id+"F5.wireOp",EDGE,"E8.34.0");Q49=makeQuery(id+"F5.imprint","IMPRINT",FACE,{"disambiguationData":[TD([[makeQuery(id+"F5.imprint","IMPRINT",EDGE,{"derivedFrom":subQ0}),1.0]])]});}
            var Q50;
            {var subQ0=sQuery(id+"F5.wireOp",EDGE,"E8.36.0");Q50=makeQuery(id+"F5.imprint","IMPRINT",FACE,{"disambiguationData":[TD([[makeQuery(id+"F5.imprint","IMPRINT",EDGE,{"derivedFrom":subQ0}),1.0]])]});}
            var Q51;
            {var subQ0=sQuery(id+"F5.wireOp",EDGE,"E8.38.0");Q51=makeQuery(id+"F5.imprint","IMPRINT",FACE,{"disambiguationData":[TD([[makeQuery(id+"F5.imprint","IMPRINT",EDGE,{"derivedFrom":subQ0}),1.0]])]});}
            var Q52;
            {var subQ0=sQuery(id+"F5.wireOp",EDGE,"E8.81.0");Q52=makeQuery(id+"F5.imprint","IMPRINT",FACE,{"disambiguationData":[TD([[makeQuery(id+"F5.imprint","IMPRINT",EDGE,{"derivedFrom":subQ0}),1.0]])]});}
            var Q53;
            {var subQ0=sQuery(id+"F5.wireOp",EDGE,"E8.65.0");Q53=makeQuery(id+"F5.imprint","IMPRINT",FACE,{"disambiguationData":[TD([[makeQuery(id+"F5.imprint","IMPRINT",EDGE,{"derivedFrom":subQ0}),1.0]])]});}
            var Q54;
            {var subQ0=sQuery(id+"F5.wireOp",EDGE,"E8.82.0");Q54=makeQuery(id+"F5.imprint","IMPRINT",FACE,{"disambiguationData":[TD([[makeQuery(id+"F5.imprint","IMPRINT",EDGE,{"derivedFrom":subQ0}),1.0]])]});}
            var Q55;
            {var subQ0=sQuery(id+"F5.wireOp",EDGE,"E8.66.0");Q55=makeQuery(id+"F5.imprint","IMPRINT",FACE,{"disambiguationData":[TD([[makeQuery(id+"F5.imprint","IMPRINT",EDGE,{"derivedFrom":subQ0}),1.0]])]});}
            var Q56;
            {var subQ0=sQuery(id+"F5.wireOp",EDGE,"E8.14.0");Q56=makeQuery(id+"F5.imprint","IMPRINT",FACE,{"disambiguationData":[TD([[makeQuery(id+"F5.imprint","IMPRINT",EDGE,{"derivedFrom":subQ0}),1.0]])]});}
            var Q57;
            {var subQ0=sQuery(id+"F5.wireOp",EDGE,"E8.94.0");Q57=makeQuery(id+"F5.imprint","IMPRINT",FACE,{"disambiguationData":[TD([[makeQuery(id+"F5.imprint","IMPRINT",EDGE,{"derivedFrom":subQ0}),1.0]])]});}
            var Q58;
            {var subQ0=sQuery(id+"F5.wireOp",EDGE,"E8.59.0");Q58=makeQuery(id+"F5.imprint","IMPRINT",FACE,{"disambiguationData":[TD([[makeQuery(id+"F5.imprint","IMPRINT",EDGE,{"derivedFrom":subQ0}),1.0]])]});}
            var Q59;
            {var subQ0=sQuery(id+"F5.wireOp",EDGE,"E8.6.0");Q59=makeQuery(id+"F5.imprint","IMPRINT",FACE,{"disambiguationData":[TD([[makeQuery(id+"F5.imprint","IMPRINT",EDGE,{"derivedFrom":subQ0}),1.0]])]});}
            var Q60;
            {var subQ0=sQuery(id+"F5.wireOp",EDGE,"E8.93.0");Q60=makeQuery(id+"F5.imprint","IMPRINT",FACE,{"disambiguationData":[TD([[makeQuery(id+"F5.imprint","IMPRINT",EDGE,{"derivedFrom":subQ0}),1.0]])]});}
            var Q61;
            {var subQ0=sQuery(id+"F5.wireOp",EDGE,"E8.9.0");Q61=makeQuery(id+"F5.imprint","IMPRINT",FACE,{"disambiguationData":[TD([[makeQuery(id+"F5.imprint","IMPRINT",EDGE,{"derivedFrom":subQ0}),1.0]])]});}
            var Q62;
            {var subQ0=sQuery(id+"F5.wireOp",EDGE,"E8.60.0");Q62=makeQuery(id+"F5.imprint","IMPRINT",FACE,{"disambiguationData":[TD([[makeQuery(id+"F5.imprint","IMPRINT",EDGE,{"derivedFrom":subQ0}),1.0]])]});}
            var Q63;
            {var subQ0=sQuery(id+"F5.wireOp",EDGE,"E8.92.0");Q63=makeQuery(id+"F5.imprint","IMPRINT",FACE,{"disambiguationData":[TD([[makeQuery(id+"F5.imprint","IMPRINT",EDGE,{"derivedFrom":subQ0}),1.0]])]});}
            var Q64;
            {var subQ0=sQuery(id+"F5.wireOp",EDGE,"E8.44.0");Q64=makeQuery(id+"F5.imprint","IMPRINT",FACE,{"disambiguationData":[TD([[makeQuery(id+"F5.imprint","IMPRINT",EDGE,{"derivedFrom":subQ0}),1.0]])]});}
            var Q65;
            {var subQ0=sQuery(id+"F5.wireOp",EDGE,"E8.8.0");Q65=makeQuery(id+"F5.imprint","IMPRINT",FACE,{"disambiguationData":[TD([[makeQuery(id+"F5.imprint","IMPRINT",EDGE,{"derivedFrom":subQ0}),1.0]])]});}
            var Q66;
            {var subQ0=sQuery(id+"F5.wireOp",EDGE,"E8.91.0");Q66=makeQuery(id+"F5.imprint","IMPRINT",FACE,{"disambiguationData":[TD([[makeQuery(id+"F5.imprint","IMPRINT",EDGE,{"derivedFrom":subQ0}),1.0]])]});}
            var Q67;
            {var subQ0=sQuery(id+"F5.wireOp",EDGE,"E8.4.0");Q67=makeQuery(id+"F5.imprint","IMPRINT",FACE,{"disambiguationData":[TD([[makeQuery(id+"F5.imprint","IMPRINT",EDGE,{"derivedFrom":subQ0}),1.0]])]});}
            var Q68;
            {var subQ0=sQuery(id+"F5.wireOp",EDGE,"E8.68.0");Q68=makeQuery(id+"F5.imprint","IMPRINT",FACE,{"disambiguationData":[TD([[makeQuery(id+"F5.imprint","IMPRINT",EDGE,{"derivedFrom":subQ0}),1.0]])]});}
            var Q69;
            {var subQ0=sQuery(id+"F5.wireOp",EDGE,"E8.84.0");Q69=makeQuery(id+"F5.imprint","IMPRINT",FACE,{"disambiguationData":[TD([[makeQuery(id+"F5.imprint","IMPRINT",EDGE,{"derivedFrom":subQ0}),1.0]])]});}
            var Q70;
            {var subQ0=sQuery(id+"F5.wireOp",EDGE,"E8.87.0");Q70=makeQuery(id+"F5.imprint","IMPRINT",FACE,{"disambiguationData":[TD([[makeQuery(id+"F5.imprint","IMPRINT",EDGE,{"derivedFrom":subQ0}),1.0]])]});}
            var Q71;
            {var subQ0=sQuery(id+"F5.wireOp",EDGE,"E8.18.0");Q71=makeQuery(id+"F5.imprint","IMPRINT",FACE,{"disambiguationData":[TD([[makeQuery(id+"F5.imprint","IMPRINT",EDGE,{"derivedFrom":subQ0}),1.0]])]});}
            var Q72;
            {var subQ0=sQuery(id+"F5.wireOp",EDGE,"E8.63.0");Q72=makeQuery(id+"F5.imprint","IMPRINT",FACE,{"disambiguationData":[TD([[makeQuery(id+"F5.imprint","IMPRINT",EDGE,{"derivedFrom":subQ0}),1.0]])]});}
            var Q73;
            {var subQ0=sQuery(id+"F5.wireOp",EDGE,"E8.11.0");Q73=makeQuery(id+"F5.imprint","IMPRINT",FACE,{"disambiguationData":[TD([[makeQuery(id+"F5.imprint","IMPRINT",EDGE,{"derivedFrom":subQ0}),1.0]])]});}
            var Q74;
            {var subQ0=sQuery(id+"F5.wireOp",EDGE,"E8.80.0");Q74=makeQuery(id+"F5.imprint","IMPRINT",FACE,{"disambiguationData":[TD([[makeQuery(id+"F5.imprint","IMPRINT",EDGE,{"derivedFrom":subQ0}),1.0]])]});}
            var Q75;
            {var subQ0=sQuery(id+"F5.wireOp",EDGE,"E8.64.0");Q75=makeQuery(id+"F5.imprint","IMPRINT",FACE,{"disambiguationData":[TD([[makeQuery(id+"F5.imprint","IMPRINT",EDGE,{"derivedFrom":subQ0}),1.0]])]});}
            var Q76;
            {var subQ0=sQuery(id+"F5.wireOp",EDGE,"E8.41.0");Q76=makeQuery(id+"F5.imprint","IMPRINT",FACE,{"disambiguationData":[TD([[makeQuery(id+"F5.imprint","IMPRINT",EDGE,{"derivedFrom":subQ0}),1.0]])]});}
            var Q77;
            {var subQ0=sQuery(id+"F5.wireOp",EDGE,"E8.35.0");Q77=makeQuery(id+"F5.imprint","IMPRINT",FACE,{"disambiguationData":[TD([[makeQuery(id+"F5.imprint","IMPRINT",EDGE,{"derivedFrom":subQ0}),1.0]])]});}
            var Q78;
            {var subQ0=sQuery(id+"F5.wireOp",EDGE,"E8.37.0");Q78=makeQuery(id+"F5.imprint","IMPRINT",FACE,{"disambiguationData":[TD([[makeQuery(id+"F5.imprint","IMPRINT",EDGE,{"derivedFrom":subQ0}),1.0]])]});}
            var Q79;
            {var subQ0=sQuery(id+"F5.wireOp",EDGE,"E8.49.0");Q79=makeQuery(id+"F5.imprint","IMPRINT",FACE,{"disambiguationData":[TD([[makeQuery(id+"F5.imprint","IMPRINT",EDGE,{"derivedFrom":subQ0}),1.0]])]});}
            var Q80;
            {var subQ0=sQuery(id+"F5.wireOp",EDGE,"E8.57.0");Q80=makeQuery(id+"F5.imprint","IMPRINT",FACE,{"disambiguationData":[TD([[makeQuery(id+"F5.imprint","IMPRINT",EDGE,{"derivedFrom":subQ0}),1.0]])]});}
            var Q81;
            {var subQ0=sQuery(id+"F5.wireOp",EDGE,"E8.5.0");Q81=makeQuery(id+"F5.imprint","IMPRINT",FACE,{"disambiguationData":[TD([[makeQuery(id+"F5.imprint","IMPRINT",EDGE,{"derivedFrom":subQ0}),1.0]])]});}
            var Q82;
            {var subQ0=sQuery(id+"F5.wireOp",EDGE,"E8.89.0");Q82=makeQuery(id+"F5.imprint","IMPRINT",FACE,{"disambiguationData":[TD([[makeQuery(id+"F5.imprint","IMPRINT",EDGE,{"derivedFrom":subQ0}),1.0]])]});}
            var Q83;
            {var subQ0=sQuery(id+"F5.wireOp",EDGE,"E8.15.0");Q83=makeQuery(id+"F5.imprint","IMPRINT",FACE,{"disambiguationData":[TD([[makeQuery(id+"F5.imprint","IMPRINT",EDGE,{"derivedFrom":subQ0}),1.0]])]});}
            var Q84;
            {var subQ0=sQuery(id+"F5.wireOp",EDGE,"E8.16.0");Q84=makeQuery(id+"F5.imprint","IMPRINT",FACE,{"disambiguationData":[TD([[makeQuery(id+"F5.imprint","IMPRINT",EDGE,{"derivedFrom":subQ0}),1.0]])]});}
            var Q85;
            {var subQ0=sQuery(id+"F5.wireOp",EDGE,"E8.52.0");Q85=makeQuery(id+"F5.imprint","IMPRINT",FACE,{"disambiguationData":[TD([[makeQuery(id+"F5.imprint","IMPRINT",EDGE,{"derivedFrom":subQ0}),1.0]])]});}
            var Q86;
            {var subQ0=sQuery(id+"F5.wireOp",EDGE,"E8.77.0");Q86=makeQuery(id+"F5.imprint","IMPRINT",FACE,{"disambiguationData":[TD([[makeQuery(id+"F5.imprint","IMPRINT",EDGE,{"derivedFrom":subQ0}),1.0]])]});}
            var Q87;
            {var subQ0=sQuery(id+"F5.wireOp",EDGE,"E8.74.0");Q87=makeQuery(id+"F5.imprint","IMPRINT",FACE,{"disambiguationData":[TD([[makeQuery(id+"F5.imprint","IMPRINT",EDGE,{"derivedFrom":subQ0}),1.0]])]});}
            var Q88;
            {var subQ0=sQuery(id+"F5.wireOp",EDGE,"E8.76.0");Q88=makeQuery(id+"F5.imprint","IMPRINT",FACE,{"disambiguationData":[TD([[makeQuery(id+"F5.imprint","IMPRINT",EDGE,{"derivedFrom":subQ0}),1.0]])]});}
            var Q89;
            {var subQ0=sQuery(id+"F5.wireOp",EDGE,"E8.42.0");Q89=makeQuery(id+"F5.imprint","IMPRINT",FACE,{"disambiguationData":[TD([[makeQuery(id+"F5.imprint","IMPRINT",EDGE,{"derivedFrom":subQ0}),1.0]])]});}
            var Q90;
            {var subQ0=sQuery(id+"F5.wireOp",EDGE,"E8.54.0");Q90=makeQuery(id+"F5.imprint","IMPRINT",FACE,{"disambiguationData":[TD([[makeQuery(id+"F5.imprint","IMPRINT",EDGE,{"derivedFrom":subQ0}),1.0]])]});}
            var Q91;
            {var subQ0=sQuery(id+"F5.wireOp",EDGE,"E7");Q91=makeQuery(id+"F5.imprint","IMPRINT",FACE,{"disambiguationData":[TD([[makeQuery(id+"F5.imprint","IMPRINT",EDGE,{"derivedFrom":subQ0}),1.0]])]});}
            var Q92;
            {var subQ0=sQuery(id+"F5.wireOp",EDGE,"E8.3.0");Q92=makeQuery(id+"F5.imprint","IMPRINT",FACE,{"disambiguationData":[TD([[makeQuery(id+"F5.imprint","IMPRINT",EDGE,{"derivedFrom":subQ0}),1.0]])]});}
            var Q93;
            {var subQ0=sQuery(id+"F5.wireOp",EDGE,"E8.55.0");Q93=makeQuery(id+"F5.imprint","IMPRINT",FACE,{"disambiguationData":[TD([[makeQuery(id+"F5.imprint","IMPRINT",EDGE,{"derivedFrom":subQ0}),1.0]])]});}
            var Q94;
            {var subQ0=sQuery(id+"F5.wireOp",EDGE,"E8.53.0");Q94=makeQuery(id+"F5.imprint","IMPRINT",FACE,{"disambiguationData":[TD([[makeQuery(id+"F5.imprint","IMPRINT",EDGE,{"derivedFrom":subQ0}),1.0]])]});}
            var Q95;
            {var subQ0=sQuery(id+"F5.wireOp",EDGE,"E8.75.0");Q95=makeQuery(id+"F5.imprint","IMPRINT",FACE,{"disambiguationData":[TD([[makeQuery(id+"F5.imprint","IMPRINT",EDGE,{"derivedFrom":subQ0}),1.0]])]});}
            var Q96;
            {var subQ0=sQuery(id+"F5.wireOp",EDGE,"E8.39.0");Q96=makeQuery(id+"F5.imprint","IMPRINT",FACE,{"disambiguationData":[TD([[makeQuery(id+"F5.imprint","IMPRINT",EDGE,{"derivedFrom":subQ0}),1.0]])]});}
            var Q97;
            {var subQ0=sQuery(id+"F5.wireOp",EDGE,"E8.40.0");Q97=makeQuery(id+"F5.imprint","IMPRINT",FACE,{"disambiguationData":[TD([[makeQuery(id+"F5.imprint","IMPRINT",EDGE,{"derivedFrom":subQ0}),1.0]])]});}
            var Q98;
            {var subQ0=sQuery(id+"F5.wireOp",EDGE,"E8.13.0");Q98=makeQuery(id+"F5.imprint","IMPRINT",FACE,{"disambiguationData":[TD([[makeQuery(id+"F5.imprint","IMPRINT",EDGE,{"derivedFrom":subQ0}),1.0]])]});}
            var Q99;
            {var subQ0=sQuery(id+"F5.wireOp",EDGE,"E8.97.0");Q99=makeQuery(id+"F5.imprint","IMPRINT",FACE,{"disambiguationData":[TD([[makeQuery(id+"F5.imprint","IMPRINT",EDGE,{"derivedFrom":subQ0}),1.0]])]});}
            var Q100;
            {var subQ0=sQuery(id+"F5.wireOp",EDGE,"E8.50.0");Q100=makeQuery(id+"F5.imprint","IMPRINT",FACE,{"disambiguationData":[TD([[makeQuery(id+"F5.imprint","IMPRINT",EDGE,{"derivedFrom":subQ0}),1.0]])]});}
            var Q101;
            {var subQ0=sQuery(id+"F5.wireOp",EDGE,"E8.98.0");Q101=makeQuery(id+"F5.imprint","IMPRINT",FACE,{"disambiguationData":[TD([[makeQuery(id+"F5.imprint","IMPRINT",EDGE,{"derivedFrom":subQ0}),1.0]])]});}
            var Q102;
            {var subQ0=sQuery(id+"F5.wireOp",EDGE,"E8.83.0");Q102=makeQuery(id+"F5.imprint","IMPRINT",FACE,{"disambiguationData":[TD([[makeQuery(id+"F5.imprint","IMPRINT",EDGE,{"derivedFrom":subQ0}),1.0]])]});}
            var Q103;
            {var subQ0=sQuery(id+"F5.wireOp",EDGE,"E8.67.0");Q103=makeQuery(id+"F5.imprint","IMPRINT",FACE,{"disambiguationData":[TD([[makeQuery(id+"F5.imprint","IMPRINT",EDGE,{"derivedFrom":subQ0}),1.0]])]});}
            var Q104;
            {var subQ0=sQuery(id+"F5.wireOp",EDGE,"E8.51.0");Q104=makeQuery(id+"F5.imprint","IMPRINT",FACE,{"disambiguationData":[TD([[makeQuery(id+"F5.imprint","IMPRINT",EDGE,{"derivedFrom":subQ0}),1.0]])]});}
            var Q105;
            {var subQ0=sQuery(id+"F5.wireOp",EDGE,"E8.99.0");Q105=makeQuery(id+"F5.imprint","IMPRINT",FACE,{"disambiguationData":[TD([[makeQuery(id+"F5.imprint","IMPRINT",EDGE,{"derivedFrom":subQ0}),1.0]])]});}
            var Q106;
            {var subQ0=sQuery(id+"F5.wireOp",EDGE,"E8.46.0");Q106=makeQuery(id+"F5.imprint","IMPRINT",FACE,{"disambiguationData":[TD([[makeQuery(id+"F5.imprint","IMPRINT",EDGE,{"derivedFrom":subQ0}),1.0]])]});}
            var Q107;
            {var subQ0=sQuery(id+"F5.wireOp",EDGE,"E8.1.0");Q107=makeQuery(id+"F5.imprint","IMPRINT",FACE,{"disambiguationData":[TD([[makeQuery(id+"F5.imprint","IMPRINT",EDGE,{"derivedFrom":subQ0}),1.0]])]});}
            var Q108;
            {var subQ0=sQuery(id+"F5.wireOp",EDGE,"E8.2.0");Q108=makeQuery(id+"F5.imprint","IMPRINT",FACE,{"disambiguationData":[TD([[makeQuery(id+"F5.imprint","IMPRINT",EDGE,{"derivedFrom":subQ0}),1.0]])]});}
            var Q109;
            {var subQ0=sQuery(id+"F5.wireOp",EDGE,"E8.62.0");Q109=makeQuery(id+"F5.imprint","IMPRINT",FACE,{"disambiguationData":[TD([[makeQuery(id+"F5.imprint","IMPRINT",EDGE,{"derivedFrom":subQ0}),1.0]])]});}
            var Q110;
            {var subQ0=sQuery(id+"F5.wireOp",EDGE,"E8.73.0");Q110=makeQuery(id+"F5.imprint","IMPRINT",FACE,{"disambiguationData":[TD([[makeQuery(id+"F5.imprint","IMPRINT",EDGE,{"derivedFrom":subQ0}),1.0]])]});}
            var Q111;
            {var subQ0=sQuery(id+"F5.wireOp",EDGE,"E8.30.0");Q111=makeQuery(id+"F5.imprint","IMPRINT",FACE,{"disambiguationData":[TD([[makeQuery(id+"F5.imprint","IMPRINT",EDGE,{"derivedFrom":subQ0}),1.0]])]});}
            var Q112;
            {var subQ0=sQuery(id+"F5.wireOp",EDGE,"E9.2.70.0");Q112=makeQuery(id+"F5.imprint","IMPRINT",FACE,{"disambiguationData":[TD([[makeQuery(id+"F5.imprint","IMPRINT",EDGE,{"derivedFrom":subQ0}),1.0]])]});}
            var Q113;
            {var subQ0=sQuery(id+"F5.wireOp",EDGE,"E9.2.71.0");Q113=makeQuery(id+"F5.imprint","IMPRINT",FACE,{"disambiguationData":[TD([[makeQuery(id+"F5.imprint","IMPRINT",EDGE,{"derivedFrom":subQ0}),1.0]])]});}
            var Q114;
            {var subQ0=sQuery(id+"F5.wireOp",EDGE,"E9.2.72.0");Q114=makeQuery(id+"F5.imprint","IMPRINT",FACE,{"disambiguationData":[TD([[makeQuery(id+"F5.imprint","IMPRINT",EDGE,{"derivedFrom":subQ0}),1.0]])]});}
            var Q115;
            {var subQ0=sQuery(id+"F5.wireOp",EDGE,"E9.2.73.0");Q115=makeQuery(id+"F5.imprint","IMPRINT",FACE,{"disambiguationData":[TD([[makeQuery(id+"F5.imprint","IMPRINT",EDGE,{"derivedFrom":subQ0}),1.0]])]});}
            var Q116;
            {var subQ0=sQuery(id+"F5.wireOp",EDGE,"E9.2.74.0");Q116=makeQuery(id+"F5.imprint","IMPRINT",FACE,{"disambiguationData":[TD([[makeQuery(id+"F5.imprint","IMPRINT",EDGE,{"derivedFrom":subQ0}),1.0]])]});}
            var Q117;
            {var subQ2=sQuery(id+"F5.wireOp",EDGE,"E0.rect.top");Q117=makeQuery(id+"F5.imprint","IMPRINT",FACE,{"disambiguationData":[TD([[makeQuery(id+"F5.imprint","IMPRINT",EDGE,{"derivedFrom":subQ2}),-1.0]])]});}
            var Q118;
            {var subQ4=sQuery(id+"F5.wireOp",EDGE,"E5.3.0");Q118=makeQuery(id+"F5.imprint","IMPRINT",FACE,{"disambiguationData":[TD([[makeQuery(id+"F5.imprint","IMPRINT",EDGE,{"derivedFrom":subQ4}),-1.0]])]});}
            var Q119;
            {var subQ1=sQuery(id+"F5.wireOp",EDGE,"E10.MirrorCS");Q119=makeQuery(id+"F5.imprint","IMPRINT",FACE,{"disambiguationData":[TD([[makeQuery(id+"F5.imprint","IMPRINT",EDGE,{"derivedFrom":subQ1}),1.0]])]});}
            var Q120;
            {var subQ5=sQuery(id+"F5.wireOp",EDGE,"E11.MirrorCS");Q120=makeQuery(id+"F5.imprint","IMPRINT",FACE,{"disambiguationData":[TD([[makeQuery(id+"F5.imprint","IMPRINT",EDGE,{"derivedFrom":subQ5}),1.0]])]});}
            var Q121;
            {var subQ1=sQuery(id+"F5.wireOp",EDGE,"E12.MirrorCS");Q121=makeQuery(id+"F5.imprint","IMPRINT",FACE,{"disambiguationData":[TD([[makeQuery(id+"F5.imprint","IMPRINT",EDGE,{"derivedFrom":subQ1}),-1.0]])]});}
            var Q122;
            {var subQ4=sQuery(id+"F5.wireOp",EDGE,"E5.3.1");Q122=makeQuery(id+"F5.imprint","IMPRINT",FACE,{"disambiguationData":[TD([[makeQuery(id+"F5.imprint","IMPRINT",EDGE,{"derivedFrom":subQ4}),1.0]])]});}
            var Q123;
            {var subQ4=sQuery(id+"F5.wireOp",EDGE,"E10.MirrorCS");Q123=makeQuery(id+"F5.imprint","IMPRINT",FACE,{"disambiguationData":[TD([[makeQuery(id+"F5.imprint","IMPRINT",EDGE,{"derivedFrom":subQ4}),-1.0]])]});}
            extrude(context, id + "F8", {"entities" : qUnion([Q0, Q1, Q2, Q3, Q4, Q5, Q6, Q7, Q8, Q9, Q10, Q11, Q12, Q13, Q14, Q15, Q16, Q17, Q18, Q19, Q20, Q21, Q22, Q23, Q24, Q25, Q26, Q27, Q28, Q29, Q30, Q31, Q32, Q33, Q34, Q35, Q36, Q37, Q38, Q39, Q40, Q41, Q42, Q43, Q44, Q45, Q46, Q47, Q48, Q49, Q50, Q51, Q52, Q53, Q54, Q55, Q56, Q57, Q58, Q59, Q60, Q61, Q62, Q63, Q64, Q65, Q66, Q67, Q68, Q69, Q70, Q71, Q72, Q73, Q74, Q75, Q76, Q77, Q78, Q79, Q80, Q81, Q82, Q83, Q84, Q85, Q86, Q87, Q88, Q89, Q90, Q91, Q92, Q93, Q94, Q95, Q96, Q97, Q98, Q99, Q100, Q101, Q102, Q103, Q104, Q105, Q106, Q107, Q108, Q109, Q110, Q111, Q112, Q113, Q114, Q115, Q116, Q117, Q118, Q119, Q120, Q121, Q122, Q123]), "operationType" : NewBodyOperationType.ADD, "oppositeDirection" : true, "depth" : (getVariable(context, 'WallThickness')) * mm});
        }
        {
            var Q0;
            {var subQ1=sQuery(id+"F5.wireOp",EDGE,"E5.3.0");Q0=makeQuery(id+"F5.imprint","IMPRINT",FACE,{"disambiguationData":[TD([[makeQuery(id+"F5.imprint","IMPRINT",EDGE,{"derivedFrom":subQ1}),1.0]])]});}
            var Q1;
            {var subQ1=sQuery(id+"F5.wireOp",EDGE,"E10.MirrorCS");Q1=makeQuery(id+"F5.imprint","IMPRINT",FACE,{"disambiguationData":[TD([[makeQuery(id+"F5.imprint","IMPRINT",EDGE,{"derivedFrom":subQ1}),1.0]])]});}
            var Q2;
            {var subQ1=sQuery(id+"F5.wireOp",EDGE,"E12.MirrorCS");Q2=makeQuery(id+"F5.imprint","IMPRINT",FACE,{"disambiguationData":[TD([[makeQuery(id+"F5.imprint","IMPRINT",EDGE,{"derivedFrom":subQ1}),-1.0]])]});}
            var Q3;
            {var subQ1=sQuery(id+"F5.wireOp",EDGE,"E14.MirrorCS");Q3=makeQuery(id+"F5.imprint","IMPRINT",FACE,{"disambiguationData":[TD([[makeQuery(id+"F5.imprint","IMPRINT",EDGE,{"derivedFrom":subQ1}),1.0]])]});}
            extrude(context, id + "F9", {"entities" : qUnion([Q0, Q1, Q2, Q3]), "operationType" : NewBodyOperationType.ADD, "depth" : (getVariable(context, 'CylinderHeight')) * mm});
        }
        {
            var Q0;
            Q0=makeQuery(id+"F9.opExtrude","CAP_EDGE",EDGE,{"disambiguationData":[OSD([sQuery(id+"F5.wireOp",EDGE,"E0.rect.right")])],"isStart":false});
            var Q1;
            Q1=makeQuery(id+"F9.opExtrude","CAP_EDGE",EDGE,{"disambiguationData":[OSD([sQuery(id+"F5.wireOp",EDGE,"E0.rect.top")])],"isStart":false});
            var Q2;
            Q2=makeQuery(id+"F9.opExtrude","CAP_EDGE",EDGE,{"disambiguationData":[OSD([sQuery(id+"F5.wireOp",EDGE,"E0.rect.left")])],"isStart":false});
            var Q3;
            Q3=makeQuery(id+"F9.opExtrude","CAP_EDGE",EDGE,{"disambiguationData":[OSD([sQuery(id+"F5.wireOp",EDGE,"E0.rect.bottom")])],"isStart":false});
            chamfer(context, id + "F10", {"entities" : qUnion([Q0, Q1, Q2, Q3]), "chamferType" : ChamferType.TWO_OFFSETS, "width1" : (getVariable(context, 'PlateWidth') - getVariable(context, 'TableLegDiameter') - (getVariable(context, 'WallThickness') * 2)) / 2 * mm, "oppositeDirection" : false, "width2" : (getVariable(context, 'CylinderHeight')) * mm, "tangentPropagation" : true});
        }
        {
            var Q0;
            Q0=sQuery(id+"F5.wireOp",VERTEX,"E16.MirrorP");
            var Q1;
            Q1=sQuery(id+"F5.wireOp",VERTEX,"E6");
            var Q2;
            Q2=sQuery(id+"F5.wireOp",VERTEX,"E17.MirrorP");
            var Q3;
            Q3=sQuery(id+"F5.wireOp",VERTEX,"E18.MirrorP");
            var Q4;
            Q4=makeQuery(id+"F7.opExtrude","SWEPT_BODY",BODY,{"disambiguationData":[OSD([sQuery(id+"F5.wireOp",EDGE,"E1"),sQuery(id+"F5.wireOp",EDGE,"E4.0")])]});
            hole(context, id + "F11", {"style" : HoleStyle.SIMPLE, "holeDiameter" : (getVariable(context, 'BoltHoleDiameter')) * mm, "endStyle" : HoleEndStyle.THROUGH, "locations" : qUnion([Q0, Q1, Q2, Q3]), "scope" : qUnion([Q4])});
        }
        {
            var Q0;
            Q0=makeQuery(id+"F8.opExtrude","SWEPT_EDGE",EDGE,{"disambiguationData":[OSD([sQuery(id+"F5.wireOp",EDGE,"E0.rect.top"),sQuery(id+"F5.wireOp",EDGE,"E0.rect.right")])]});
            var Q1;
            Q1=makeQuery(id+"F8.opExtrude","SWEPT_EDGE",EDGE,{"disambiguationData":[OSD([sQuery(id+"F5.wireOp",EDGE,"E0.rect.bottom"),sQuery(id+"F5.wireOp",EDGE,"E0.rect.right")])]});
            var Q2;
            Q2=makeQuery(id+"F8.opExtrude","SWEPT_EDGE",EDGE,{"disambiguationData":[OSD([sQuery(id+"F5.wireOp",EDGE,"E0.rect.top"),sQuery(id+"F5.wireOp",EDGE,"E0.rect.left")])]});
            var Q3;
            Q3=makeQuery(id+"F8.opExtrude","SWEPT_EDGE",EDGE,{"disambiguationData":[OSD([sQuery(id+"F5.wireOp",EDGE,"E0.rect.bottom"),sQuery(id+"F5.wireOp",EDGE,"E0.rect.left")])]});
            var Q4;
            Q4=makeQuery(id+"F10.opChamfer","BLEND_EDGE",EDGE,{"blendedFrom":[makeQuery(id+"F9.opExtrude","CAP_EDGE",EDGE,{"disambiguationData":[OSD([sQuery(id+"F5.wireOp",EDGE,"E0.rect.right")])],"isStart":false}),makeQuery(id+"F9.opExtrude","SWEPT_FACE",FACE,{"disambiguationData":[OSD([sQuery(id+"F5.wireOp",EDGE,"E5.3.1")])]})],"blendedInto":[makeQuery(id+"F9.opExtrude","SWEPT_FACE",FACE,{"disambiguationData":[OSD([sQuery(id+"F5.wireOp",EDGE,"E5.3.1")])]})]});
            var Q5;
            Q5=makeQuery(id+"F10.opChamfer","BLEND_EDGE",EDGE,{"blendedFrom":[makeQuery(id+"F9.opExtrude","CAP_EDGE",EDGE,{"disambiguationData":[OSD([sQuery(id+"F5.wireOp",EDGE,"E0.rect.right")])],"isStart":false}),makeQuery(id+"F9.opExtrude","SWEPT_FACE",FACE,{"disambiguationData":[OSD([sQuery(id+"F5.wireOp",EDGE,"E5.3.0")])]})],"blendedInto":[makeQuery(id+"F9.opExtrude","SWEPT_FACE",FACE,{"disambiguationData":[OSD([sQuery(id+"F5.wireOp",EDGE,"E5.3.0")])]})]});
            var Q6;
            Q6=makeQuery(id+"F13.opFillet","BLEND_EDGE",EDGE,{"blendedFrom":[makeQuery(id+"F9.opExtrude","SWEPT_EDGE",EDGE,{"disambiguationData":[OSD([sQuery(id+"F5.wireOp",EDGE,"E4.0"),sQuery(id+"F5.wireOp",EDGE,"E14.MirrorCS")])]}),makeQuery(id+"F10.opChamfer","BLEND_FACE",FACE,{"disambiguationData":[OSD([sQuery(id+"F5.wireOp",EDGE,"E0.rect.top")])]})],"blendedInto":[makeQuery(id+"F10.opChamfer","BLEND_FACE",FACE,{"disambiguationData":[OSD([sQuery(id+"F5.wireOp",EDGE,"E0.rect.top")])]})]});
            var Q7;
            Q7=makeQuery(id+"F13.opFillet","BLEND_EDGE",EDGE,{"blendedFrom":[makeQuery(id+"F9.opExtrude","SWEPT_EDGE",EDGE,{"disambiguationData":[OSD([sQuery(id+"F5.wireOp",EDGE,"E4.0"),sQuery(id+"F5.wireOp",EDGE,"E15.MirrorCS")])]}),makeQuery(id+"F10.opChamfer","BLEND_FACE",FACE,{"disambiguationData":[OSD([sQuery(id+"F5.wireOp",EDGE,"E0.rect.top")])]})],"blendedInto":[makeQuery(id+"F10.opChamfer","BLEND_FACE",FACE,{"disambiguationData":[OSD([sQuery(id+"F5.wireOp",EDGE,"E0.rect.top")])]})]});
            var Q8;
            Q8=makeQuery(id+"F10.opChamfer","BLEND_EDGE",EDGE,{"blendedFrom":[makeQuery(id+"F9.opExtrude","CAP_EDGE",EDGE,{"disambiguationData":[OSD([sQuery(id+"F5.wireOp",EDGE,"E0.rect.left")])],"isStart":false}),makeQuery(id+"F9.opExtrude","SWEPT_FACE",FACE,{"disambiguationData":[OSD([sQuery(id+"F5.wireOp",EDGE,"E10.MirrorCS")])]})],"blendedInto":[makeQuery(id+"F9.opExtrude","SWEPT_FACE",FACE,{"disambiguationData":[OSD([sQuery(id+"F5.wireOp",EDGE,"E10.MirrorCS")])]})]});
            var Q9;
            Q9=makeQuery(id+"F10.opChamfer","BLEND_EDGE",EDGE,{"blendedFrom":[makeQuery(id+"F9.opExtrude","CAP_EDGE",EDGE,{"disambiguationData":[OSD([sQuery(id+"F5.wireOp",EDGE,"E0.rect.left")])],"isStart":false}),makeQuery(id+"F9.opExtrude","SWEPT_FACE",FACE,{"disambiguationData":[OSD([sQuery(id+"F5.wireOp",EDGE,"E11.MirrorCS")])]})],"blendedInto":[makeQuery(id+"F9.opExtrude","SWEPT_FACE",FACE,{"disambiguationData":[OSD([sQuery(id+"F5.wireOp",EDGE,"E11.MirrorCS")])]})]});
            var Q10;
            Q10=makeQuery(id+"F13.opFillet","BLEND_EDGE",EDGE,{"blendedFrom":[makeQuery(id+"F9.opExtrude","SWEPT_EDGE",EDGE,{"disambiguationData":[OSD([sQuery(id+"F5.wireOp",EDGE,"E4.0"),sQuery(id+"F5.wireOp",EDGE,"E13.MirrorCS")])]}),makeQuery(id+"F10.opChamfer","BLEND_FACE",FACE,{"disambiguationData":[OSD([sQuery(id+"F5.wireOp",EDGE,"E0.rect.bottom")])]})],"blendedInto":[makeQuery(id+"F10.opChamfer","BLEND_FACE",FACE,{"disambiguationData":[OSD([sQuery(id+"F5.wireOp",EDGE,"E0.rect.bottom")])]})]});
            var Q11;
            Q11=makeQuery(id+"F13.opFillet","BLEND_EDGE",EDGE,{"blendedFrom":[makeQuery(id+"F9.opExtrude","SWEPT_EDGE",EDGE,{"disambiguationData":[OSD([sQuery(id+"F5.wireOp",EDGE,"E4.0"),sQuery(id+"F5.wireOp",EDGE,"E12.MirrorCS")])]}),makeQuery(id+"F10.opChamfer","BLEND_FACE",FACE,{"disambiguationData":[OSD([sQuery(id+"F5.wireOp",EDGE,"E0.rect.bottom")])]})],"blendedInto":[makeQuery(id+"F10.opChamfer","BLEND_FACE",FACE,{"disambiguationData":[OSD([sQuery(id+"F5.wireOp",EDGE,"E0.rect.bottom")])]})]});
            var Q12;
            {var subQ0=sQuery(id+"F5.wireOp",EDGE,"E0.rect.right");var subQ1=sQuery(id+"F5.wireOp",EDGE,"E4.0");Q12=makeQuery(id+"F10.opChamfer","BLEND_EDGE",EDGE,{"blendedFrom":[makeQuery(id+"F9.opExtrude","CAP_EDGE",EDGE,{"disambiguationData":[OSD([subQ0])],"isStart":false}),makeQuery(id+"F9.boolean.opBoolean","MERGE",FACE,{"derivedFrom":[makeQuery(id+"F7.opExtrude","CAP_FACE",FACE,{"disambiguationData":[OSD([sQuery(id+"F5.wireOp",EDGE,"E1"),subQ1,sQuery(id+"F5.wireOp",EDGE,"E7"),sQuery(id+"F5.wireOp",EDGE,"E8.1.0"),sQuery(id+"F5.wireOp",EDGE,"E8.2.0"),sQuery(id+"F5.wireOp",EDGE,"E8.3.0"),sQuery(id+"F5.wireOp",EDGE,"E8.4.0"),sQuery(id+"F5.wireOp",EDGE,"E8.5.0"),sQuery(id+"F5.wireOp",EDGE,"E8.6.0"),sQuery(id+"F5.wireOp",EDGE,"E8.7.0"),sQuery(id+"F5.wireOp",EDGE,"E8.8.0"),sQuery(id+"F5.wireOp",EDGE,"E8.9.0"),sQuery(id+"F5.wireOp",EDGE,"E8.10.0"),sQuery(id+"F5.wireOp",EDGE,"E8.11.0"),sQuery(id+"F5.wireOp",EDGE,"E8.12.0"),sQuery(id+"F5.wireOp",EDGE,"E8.13.0"),sQuery(id+"F5.wireOp",EDGE,"E8.14.0"),sQuery(id+"F5.wireOp",EDGE,"E8.15.0"),sQuery(id+"F5.wireOp",EDGE,"E8.16.0"),sQuery(id+"F5.wireOp",EDGE,"E8.17.0"),sQuery(id+"F5.wireOp",EDGE,"E8.18.0"),sQuery(id+"F5.wireOp",EDGE,"E8.19.0"),sQuery(id+"F5.wireOp",EDGE,"E8.20.0"),sQuery(id+"F5.wireOp",EDGE,"E8.21.0"),sQuery(id+"F5.wireOp",EDGE,"E8.22.0"),sQuery(id+"F5.wireOp",EDGE,"E8.23.0"),sQuery(id+"F5.wireOp",EDGE,"E8.24.0"),sQuery(id+"F5.wireOp",EDGE,"E8.25.0"),sQuery(id+"F5.wireOp",EDGE,"E8.26.0"),sQuery(id+"F5.wireOp",EDGE,"E8.27.0"),sQuery(id+"F5.wireOp",EDGE,"E8.28.0"),sQuery(id+"F5.wireOp",EDGE,"E8.29.0"),sQuery(id+"F5.wireOp",EDGE,"E8.30.0"),sQuery(id+"F5.wireOp",EDGE,"E8.31.0"),sQuery(id+"F5.wireOp",EDGE,"E8.32.0"),sQuery(id+"F5.wireOp",EDGE,"E8.33.0"),sQuery(id+"F5.wireOp",EDGE,"E8.34.0"),sQuery(id+"F5.wireOp",EDGE,"E8.35.0"),sQuery(id+"F5.wireOp",EDGE,"E8.36.0"),sQuery(id+"F5.wireOp",EDGE,"E8.37.0"),sQuery(id+"F5.wireOp",EDGE,"E8.38.0"),sQuery(id+"F5.wireOp",EDGE,"E8.39.0"),sQuery(id+"F5.wireOp",EDGE,"E8.40.0"),sQuery(id+"F5.wireOp",EDGE,"E8.41.0"),sQuery(id+"F5.wireOp",EDGE,"E8.42.0"),sQuery(id+"F5.wireOp",EDGE,"E8.43.0"),sQuery(id+"F5.wireOp",EDGE,"E8.44.0"),sQuery(id+"F5.wireOp",EDGE,"E8.45.0"),sQuery(id+"F5.wireOp",EDGE,"E8.46.0"),sQuery(id+"F5.wireOp",EDGE,"E8.47.0"),sQuery(id+"F5.wireOp",EDGE,"E8.48.0"),sQuery(id+"F5.wireOp",EDGE,"E8.49.0"),sQuery(id+"F5.wireOp",EDGE,"E8.50.0"),sQuery(id+"F5.wireOp",EDGE,"E8.51.0"),sQuery(id+"F5.wireOp",EDGE,"E8.52.0"),sQuery(id+"F5.wireOp",EDGE,"E8.53.0"),sQuery(id+"F5.wireOp",EDGE,"E8.54.0"),sQuery(id+"F5.wireOp",EDGE,"E8.55.0"),sQuery(id+"F5.wireOp",EDGE,"E8.56.0"),sQuery(id+"F5.wireOp",EDGE,"E8.57.0"),sQuery(id+"F5.wireOp",EDGE,"E8.58.0"),sQuery(id+"F5.wireOp",EDGE,"E8.59.0"),sQuery(id+"F5.wireOp",EDGE,"E8.60.0"),sQuery(id+"F5.wireOp",EDGE,"E8.61.0"),sQuery(id+"F5.wireOp",EDGE,"E8.62.0"),sQuery(id+"F5.wireOp",EDGE,"E8.63.0"),sQuery(id+"F5.wireOp",EDGE,"E8.64.0"),sQuery(id+"F5.wireOp",EDGE,"E8.65.0"),sQuery(id+"F5.wireOp",EDGE,"E8.66.0"),sQuery(id+"F5.wireOp",EDGE,"E8.67.0"),sQuery(id+"F5.wireOp",EDGE,"E8.68.0"),sQuery(id+"F5.wireOp",EDGE,"E8.69.0"),sQuery(id+"F5.wireOp",EDGE,"E9.2.70.0"),sQuery(id+"F5.wireOp",EDGE,"E9.2.71.0"),sQuery(id+"F5.wireOp",EDGE,"E9.2.72.0"),sQuery(id+"F5.wireOp",EDGE,"E9.2.73.0"),sQuery(id+"F5.wireOp",EDGE,"E9.2.74.0")])],"isStart":false}),makeQuery(id+"F9.opExtrude","CAP_FACE",FACE,{"disambiguationData":[OSD([sQuery(id+"F5.wireOp",EDGE,"E0.rect.bottom"),subQ1,sQuery(id+"F5.wireOp",EDGE,"E12.MirrorCS"),sQuery(id+"F5.wireOp",EDGE,"E13.MirrorCS")])],"isStart":false}),makeQuery(id+"F9.opExtrude","CAP_FACE",FACE,{"disambiguationData":[OSD([sQuery(id+"F5.wireOp",EDGE,"E0.rect.top"),subQ1,sQuery(id+"F5.wireOp",EDGE,"E14.MirrorCS"),sQuery(id+"F5.wireOp",EDGE,"E15.MirrorCS")])],"isStart":false}),makeQuery(id+"F9.opExtrude","CAP_FACE",FACE,{"disambiguationData":[OSD([sQuery(id+"F5.wireOp",EDGE,"E0.rect.left"),subQ1,sQuery(id+"F5.wireOp",EDGE,"E10.MirrorCS"),sQuery(id+"F5.wireOp",EDGE,"E11.MirrorCS")])],"isStart":false}),makeQuery(id+"F9.opExtrude","CAP_FACE",FACE,{"disambiguationData":[OSD([subQ0,subQ1,sQuery(id+"F5.wireOp",EDGE,"E5.3.0"),sQuery(id+"F5.wireOp",EDGE,"E5.3.1")])],"isStart":false})]})],"blendedInto":[makeQuery(id+"F9.boolean.opBoolean","MERGE",FACE,{"derivedFrom":[makeQuery(id+"F7.opExtrude","CAP_FACE",FACE,{"disambiguationData":[OSD([sQuery(id+"F5.wireOp",EDGE,"E1"),subQ1,sQuery(id+"F5.wireOp",EDGE,"E7"),sQuery(id+"F5.wireOp",EDGE,"E8.1.0"),sQuery(id+"F5.wireOp",EDGE,"E8.2.0"),sQuery(id+"F5.wireOp",EDGE,"E8.3.0"),sQuery(id+"F5.wireOp",EDGE,"E8.4.0"),sQuery(id+"F5.wireOp",EDGE,"E8.5.0"),sQuery(id+"F5.wireOp",EDGE,"E8.6.0"),sQuery(id+"F5.wireOp",EDGE,"E8.7.0"),sQuery(id+"F5.wireOp",EDGE,"E8.8.0"),sQuery(id+"F5.wireOp",EDGE,"E8.9.0"),sQuery(id+"F5.wireOp",EDGE,"E8.10.0"),sQuery(id+"F5.wireOp",EDGE,"E8.11.0"),sQuery(id+"F5.wireOp",EDGE,"E8.12.0"),sQuery(id+"F5.wireOp",EDGE,"E8.13.0"),sQuery(id+"F5.wireOp",EDGE,"E8.14.0"),sQuery(id+"F5.wireOp",EDGE,"E8.15.0"),sQuery(id+"F5.wireOp",EDGE,"E8.16.0"),sQuery(id+"F5.wireOp",EDGE,"E8.17.0"),sQuery(id+"F5.wireOp",EDGE,"E8.18.0"),sQuery(id+"F5.wireOp",EDGE,"E8.19.0"),sQuery(id+"F5.wireOp",EDGE,"E8.20.0"),sQuery(id+"F5.wireOp",EDGE,"E8.21.0"),sQuery(id+"F5.wireOp",EDGE,"E8.22.0"),sQuery(id+"F5.wireOp",EDGE,"E8.23.0"),sQuery(id+"F5.wireOp",EDGE,"E8.24.0"),sQuery(id+"F5.wireOp",EDGE,"E8.25.0"),sQuery(id+"F5.wireOp",EDGE,"E8.26.0"),sQuery(id+"F5.wireOp",EDGE,"E8.27.0"),sQuery(id+"F5.wireOp",EDGE,"E8.28.0"),sQuery(id+"F5.wireOp",EDGE,"E8.29.0"),sQuery(id+"F5.wireOp",EDGE,"E8.30.0"),sQuery(id+"F5.wireOp",EDGE,"E8.31.0"),sQuery(id+"F5.wireOp",EDGE,"E8.32.0"),sQuery(id+"F5.wireOp",EDGE,"E8.33.0"),sQuery(id+"F5.wireOp",EDGE,"E8.34.0"),sQuery(id+"F5.wireOp",EDGE,"E8.35.0"),sQuery(id+"F5.wireOp",EDGE,"E8.36.0"),sQuery(id+"F5.wireOp",EDGE,"E8.37.0"),sQuery(id+"F5.wireOp",EDGE,"E8.38.0"),sQuery(id+"F5.wireOp",EDGE,"E8.39.0"),sQuery(id+"F5.wireOp",EDGE,"E8.40.0"),sQuery(id+"F5.wireOp",EDGE,"E8.41.0"),sQuery(id+"F5.wireOp",EDGE,"E8.42.0"),sQuery(id+"F5.wireOp",EDGE,"E8.43.0"),sQuery(id+"F5.wireOp",EDGE,"E8.44.0"),sQuery(id+"F5.wireOp",EDGE,"E8.45.0"),sQuery(id+"F5.wireOp",EDGE,"E8.46.0"),sQuery(id+"F5.wireOp",EDGE,"E8.47.0"),sQuery(id+"F5.wireOp",EDGE,"E8.48.0"),sQuery(id+"F5.wireOp",EDGE,"E8.49.0"),sQuery(id+"F5.wireOp",EDGE,"E8.50.0"),sQuery(id+"F5.wireOp",EDGE,"E8.51.0"),sQuery(id+"F5.wireOp",EDGE,"E8.52.0"),sQuery(id+"F5.wireOp",EDGE,"E8.53.0"),sQuery(id+"F5.wireOp",EDGE,"E8.54.0"),sQuery(id+"F5.wireOp",EDGE,"E8.55.0"),sQuery(id+"F5.wireOp",EDGE,"E8.56.0"),sQuery(id+"F5.wireOp",EDGE,"E8.57.0"),sQuery(id+"F5.wireOp",EDGE,"E8.58.0"),sQuery(id+"F5.wireOp",EDGE,"E8.59.0"),sQuery(id+"F5.wireOp",EDGE,"E8.60.0"),sQuery(id+"F5.wireOp",EDGE,"E8.61.0"),sQuery(id+"F5.wireOp",EDGE,"E8.62.0"),sQuery(id+"F5.wireOp",EDGE,"E8.63.0"),sQuery(id+"F5.wireOp",EDGE,"E8.64.0"),sQuery(id+"F5.wireOp",EDGE,"E8.65.0"),sQuery(id+"F5.wireOp",EDGE,"E8.66.0"),sQuery(id+"F5.wireOp",EDGE,"E8.67.0"),sQuery(id+"F5.wireOp",EDGE,"E8.68.0"),sQuery(id+"F5.wireOp",EDGE,"E8.69.0"),sQuery(id+"F5.wireOp",EDGE,"E9.2.70.0"),sQuery(id+"F5.wireOp",EDGE,"E9.2.71.0"),sQuery(id+"F5.wireOp",EDGE,"E9.2.72.0"),sQuery(id+"F5.wireOp",EDGE,"E9.2.73.0"),sQuery(id+"F5.wireOp",EDGE,"E9.2.74.0")])],"isStart":false}),makeQuery(id+"F9.opExtrude","CAP_FACE",FACE,{"disambiguationData":[OSD([sQuery(id+"F5.wireOp",EDGE,"E0.rect.bottom"),subQ1,sQuery(id+"F5.wireOp",EDGE,"E12.MirrorCS"),sQuery(id+"F5.wireOp",EDGE,"E13.MirrorCS")])],"isStart":false}),makeQuery(id+"F9.opExtrude","CAP_FACE",FACE,{"disambiguationData":[OSD([sQuery(id+"F5.wireOp",EDGE,"E0.rect.top"),subQ1,sQuery(id+"F5.wireOp",EDGE,"E14.MirrorCS"),sQuery(id+"F5.wireOp",EDGE,"E15.MirrorCS")])],"isStart":false}),makeQuery(id+"F9.opExtrude","CAP_FACE",FACE,{"disambiguationData":[OSD([sQuery(id+"F5.wireOp",EDGE,"E0.rect.left"),subQ1,sQuery(id+"F5.wireOp",EDGE,"E10.MirrorCS"),sQuery(id+"F5.wireOp",EDGE,"E11.MirrorCS")])],"isStart":false}),makeQuery(id+"F9.opExtrude","CAP_FACE",FACE,{"disambiguationData":[OSD([subQ0,subQ1,sQuery(id+"F5.wireOp",EDGE,"E5.3.0"),sQuery(id+"F5.wireOp",EDGE,"E5.3.1")])],"isStart":false})]})]});}
            var Q13;
            {var subQ0=sQuery(id+"F5.wireOp",EDGE,"E0.rect.left");var subQ1=sQuery(id+"F5.wireOp",EDGE,"E4.0");Q13=makeQuery(id+"F10.opChamfer","BLEND_EDGE",EDGE,{"blendedFrom":[makeQuery(id+"F9.opExtrude","CAP_EDGE",EDGE,{"disambiguationData":[OSD([subQ0])],"isStart":false}),makeQuery(id+"F9.boolean.opBoolean","MERGE",FACE,{"derivedFrom":[makeQuery(id+"F7.opExtrude","CAP_FACE",FACE,{"disambiguationData":[OSD([sQuery(id+"F5.wireOp",EDGE,"E1"),subQ1,sQuery(id+"F5.wireOp",EDGE,"E7"),sQuery(id+"F5.wireOp",EDGE,"E8.1.0"),sQuery(id+"F5.wireOp",EDGE,"E8.2.0"),sQuery(id+"F5.wireOp",EDGE,"E8.3.0"),sQuery(id+"F5.wireOp",EDGE,"E8.4.0"),sQuery(id+"F5.wireOp",EDGE,"E8.5.0"),sQuery(id+"F5.wireOp",EDGE,"E8.6.0"),sQuery(id+"F5.wireOp",EDGE,"E8.7.0"),sQuery(id+"F5.wireOp",EDGE,"E8.8.0"),sQuery(id+"F5.wireOp",EDGE,"E8.9.0"),sQuery(id+"F5.wireOp",EDGE,"E8.10.0"),sQuery(id+"F5.wireOp",EDGE,"E8.11.0"),sQuery(id+"F5.wireOp",EDGE,"E8.12.0"),sQuery(id+"F5.wireOp",EDGE,"E8.13.0"),sQuery(id+"F5.wireOp",EDGE,"E8.14.0"),sQuery(id+"F5.wireOp",EDGE,"E8.15.0"),sQuery(id+"F5.wireOp",EDGE,"E8.16.0"),sQuery(id+"F5.wireOp",EDGE,"E8.17.0"),sQuery(id+"F5.wireOp",EDGE,"E8.18.0"),sQuery(id+"F5.wireOp",EDGE,"E8.19.0"),sQuery(id+"F5.wireOp",EDGE,"E8.20.0"),sQuery(id+"F5.wireOp",EDGE,"E8.21.0"),sQuery(id+"F5.wireOp",EDGE,"E8.22.0"),sQuery(id+"F5.wireOp",EDGE,"E8.23.0"),sQuery(id+"F5.wireOp",EDGE,"E8.24.0"),sQuery(id+"F5.wireOp",EDGE,"E8.25.0"),sQuery(id+"F5.wireOp",EDGE,"E8.26.0"),sQuery(id+"F5.wireOp",EDGE,"E8.27.0"),sQuery(id+"F5.wireOp",EDGE,"E8.28.0"),sQuery(id+"F5.wireOp",EDGE,"E8.29.0"),sQuery(id+"F5.wireOp",EDGE,"E8.30.0"),sQuery(id+"F5.wireOp",EDGE,"E8.31.0"),sQuery(id+"F5.wireOp",EDGE,"E8.32.0"),sQuery(id+"F5.wireOp",EDGE,"E8.33.0"),sQuery(id+"F5.wireOp",EDGE,"E8.34.0"),sQuery(id+"F5.wireOp",EDGE,"E8.35.0"),sQuery(id+"F5.wireOp",EDGE,"E8.36.0"),sQuery(id+"F5.wireOp",EDGE,"E8.37.0"),sQuery(id+"F5.wireOp",EDGE,"E8.38.0"),sQuery(id+"F5.wireOp",EDGE,"E8.39.0"),sQuery(id+"F5.wireOp",EDGE,"E8.40.0"),sQuery(id+"F5.wireOp",EDGE,"E8.41.0"),sQuery(id+"F5.wireOp",EDGE,"E8.42.0"),sQuery(id+"F5.wireOp",EDGE,"E8.43.0"),sQuery(id+"F5.wireOp",EDGE,"E8.44.0"),sQuery(id+"F5.wireOp",EDGE,"E8.45.0"),sQuery(id+"F5.wireOp",EDGE,"E8.46.0"),sQuery(id+"F5.wireOp",EDGE,"E8.47.0"),sQuery(id+"F5.wireOp",EDGE,"E8.48.0"),sQuery(id+"F5.wireOp",EDGE,"E8.49.0"),sQuery(id+"F5.wireOp",EDGE,"E8.50.0"),sQuery(id+"F5.wireOp",EDGE,"E8.51.0"),sQuery(id+"F5.wireOp",EDGE,"E8.52.0"),sQuery(id+"F5.wireOp",EDGE,"E8.53.0"),sQuery(id+"F5.wireOp",EDGE,"E8.54.0"),sQuery(id+"F5.wireOp",EDGE,"E8.55.0"),sQuery(id+"F5.wireOp",EDGE,"E8.56.0"),sQuery(id+"F5.wireOp",EDGE,"E8.57.0"),sQuery(id+"F5.wireOp",EDGE,"E8.58.0"),sQuery(id+"F5.wireOp",EDGE,"E8.59.0"),sQuery(id+"F5.wireOp",EDGE,"E8.60.0"),sQuery(id+"F5.wireOp",EDGE,"E8.61.0"),sQuery(id+"F5.wireOp",EDGE,"E8.62.0"),sQuery(id+"F5.wireOp",EDGE,"E8.63.0"),sQuery(id+"F5.wireOp",EDGE,"E8.64.0"),sQuery(id+"F5.wireOp",EDGE,"E8.65.0"),sQuery(id+"F5.wireOp",EDGE,"E8.66.0"),sQuery(id+"F5.wireOp",EDGE,"E8.67.0"),sQuery(id+"F5.wireOp",EDGE,"E8.68.0"),sQuery(id+"F5.wireOp",EDGE,"E8.69.0"),sQuery(id+"F5.wireOp",EDGE,"E9.2.70.0"),sQuery(id+"F5.wireOp",EDGE,"E9.2.71.0"),sQuery(id+"F5.wireOp",EDGE,"E9.2.72.0"),sQuery(id+"F5.wireOp",EDGE,"E9.2.73.0"),sQuery(id+"F5.wireOp",EDGE,"E9.2.74.0")])],"isStart":false}),makeQuery(id+"F9.opExtrude","CAP_FACE",FACE,{"disambiguationData":[OSD([sQuery(id+"F5.wireOp",EDGE,"E0.rect.bottom"),subQ1,sQuery(id+"F5.wireOp",EDGE,"E12.MirrorCS"),sQuery(id+"F5.wireOp",EDGE,"E13.MirrorCS")])],"isStart":false}),makeQuery(id+"F9.opExtrude","CAP_FACE",FACE,{"disambiguationData":[OSD([sQuery(id+"F5.wireOp",EDGE,"E0.rect.top"),subQ1,sQuery(id+"F5.wireOp",EDGE,"E14.MirrorCS"),sQuery(id+"F5.wireOp",EDGE,"E15.MirrorCS")])],"isStart":false}),makeQuery(id+"F9.opExtrude","CAP_FACE",FACE,{"disambiguationData":[OSD([subQ0,subQ1,sQuery(id+"F5.wireOp",EDGE,"E10.MirrorCS"),sQuery(id+"F5.wireOp",EDGE,"E11.MirrorCS")])],"isStart":false}),makeQuery(id+"F9.opExtrude","CAP_FACE",FACE,{"disambiguationData":[OSD([sQuery(id+"F5.wireOp",EDGE,"E0.rect.right"),subQ1,sQuery(id+"F5.wireOp",EDGE,"E5.3.0"),sQuery(id+"F5.wireOp",EDGE,"E5.3.1")])],"isStart":false})]})],"blendedInto":[makeQuery(id+"F9.boolean.opBoolean","MERGE",FACE,{"derivedFrom":[makeQuery(id+"F7.opExtrude","CAP_FACE",FACE,{"disambiguationData":[OSD([sQuery(id+"F5.wireOp",EDGE,"E1"),subQ1,sQuery(id+"F5.wireOp",EDGE,"E7"),sQuery(id+"F5.wireOp",EDGE,"E8.1.0"),sQuery(id+"F5.wireOp",EDGE,"E8.2.0"),sQuery(id+"F5.wireOp",EDGE,"E8.3.0"),sQuery(id+"F5.wireOp",EDGE,"E8.4.0"),sQuery(id+"F5.wireOp",EDGE,"E8.5.0"),sQuery(id+"F5.wireOp",EDGE,"E8.6.0"),sQuery(id+"F5.wireOp",EDGE,"E8.7.0"),sQuery(id+"F5.wireOp",EDGE,"E8.8.0"),sQuery(id+"F5.wireOp",EDGE,"E8.9.0"),sQuery(id+"F5.wireOp",EDGE,"E8.10.0"),sQuery(id+"F5.wireOp",EDGE,"E8.11.0"),sQuery(id+"F5.wireOp",EDGE,"E8.12.0"),sQuery(id+"F5.wireOp",EDGE,"E8.13.0"),sQuery(id+"F5.wireOp",EDGE,"E8.14.0"),sQuery(id+"F5.wireOp",EDGE,"E8.15.0"),sQuery(id+"F5.wireOp",EDGE,"E8.16.0"),sQuery(id+"F5.wireOp",EDGE,"E8.17.0"),sQuery(id+"F5.wireOp",EDGE,"E8.18.0"),sQuery(id+"F5.wireOp",EDGE,"E8.19.0"),sQuery(id+"F5.wireOp",EDGE,"E8.20.0"),sQuery(id+"F5.wireOp",EDGE,"E8.21.0"),sQuery(id+"F5.wireOp",EDGE,"E8.22.0"),sQuery(id+"F5.wireOp",EDGE,"E8.23.0"),sQuery(id+"F5.wireOp",EDGE,"E8.24.0"),sQuery(id+"F5.wireOp",EDGE,"E8.25.0"),sQuery(id+"F5.wireOp",EDGE,"E8.26.0"),sQuery(id+"F5.wireOp",EDGE,"E8.27.0"),sQuery(id+"F5.wireOp",EDGE,"E8.28.0"),sQuery(id+"F5.wireOp",EDGE,"E8.29.0"),sQuery(id+"F5.wireOp",EDGE,"E8.30.0"),sQuery(id+"F5.wireOp",EDGE,"E8.31.0"),sQuery(id+"F5.wireOp",EDGE,"E8.32.0"),sQuery(id+"F5.wireOp",EDGE,"E8.33.0"),sQuery(id+"F5.wireOp",EDGE,"E8.34.0"),sQuery(id+"F5.wireOp",EDGE,"E8.35.0"),sQuery(id+"F5.wireOp",EDGE,"E8.36.0"),sQuery(id+"F5.wireOp",EDGE,"E8.37.0"),sQuery(id+"F5.wireOp",EDGE,"E8.38.0"),sQuery(id+"F5.wireOp",EDGE,"E8.39.0"),sQuery(id+"F5.wireOp",EDGE,"E8.40.0"),sQuery(id+"F5.wireOp",EDGE,"E8.41.0"),sQuery(id+"F5.wireOp",EDGE,"E8.42.0"),sQuery(id+"F5.wireOp",EDGE,"E8.43.0"),sQuery(id+"F5.wireOp",EDGE,"E8.44.0"),sQuery(id+"F5.wireOp",EDGE,"E8.45.0"),sQuery(id+"F5.wireOp",EDGE,"E8.46.0"),sQuery(id+"F5.wireOp",EDGE,"E8.47.0"),sQuery(id+"F5.wireOp",EDGE,"E8.48.0"),sQuery(id+"F5.wireOp",EDGE,"E8.49.0"),sQuery(id+"F5.wireOp",EDGE,"E8.50.0"),sQuery(id+"F5.wireOp",EDGE,"E8.51.0"),sQuery(id+"F5.wireOp",EDGE,"E8.52.0"),sQuery(id+"F5.wireOp",EDGE,"E8.53.0"),sQuery(id+"F5.wireOp",EDGE,"E8.54.0"),sQuery(id+"F5.wireOp",EDGE,"E8.55.0"),sQuery(id+"F5.wireOp",EDGE,"E8.56.0"),sQuery(id+"F5.wireOp",EDGE,"E8.57.0"),sQuery(id+"F5.wireOp",EDGE,"E8.58.0"),sQuery(id+"F5.wireOp",EDGE,"E8.59.0"),sQuery(id+"F5.wireOp",EDGE,"E8.60.0"),sQuery(id+"F5.wireOp",EDGE,"E8.61.0"),sQuery(id+"F5.wireOp",EDGE,"E8.62.0"),sQuery(id+"F5.wireOp",EDGE,"E8.63.0"),sQuery(id+"F5.wireOp",EDGE,"E8.64.0"),sQuery(id+"F5.wireOp",EDGE,"E8.65.0"),sQuery(id+"F5.wireOp",EDGE,"E8.66.0"),sQuery(id+"F5.wireOp",EDGE,"E8.67.0"),sQuery(id+"F5.wireOp",EDGE,"E8.68.0"),sQuery(id+"F5.wireOp",EDGE,"E8.69.0"),sQuery(id+"F5.wireOp",EDGE,"E9.2.70.0"),sQuery(id+"F5.wireOp",EDGE,"E9.2.71.0"),sQuery(id+"F5.wireOp",EDGE,"E9.2.72.0"),sQuery(id+"F5.wireOp",EDGE,"E9.2.73.0"),sQuery(id+"F5.wireOp",EDGE,"E9.2.74.0")])],"isStart":false}),makeQuery(id+"F9.opExtrude","CAP_FACE",FACE,{"disambiguationData":[OSD([sQuery(id+"F5.wireOp",EDGE,"E0.rect.bottom"),subQ1,sQuery(id+"F5.wireOp",EDGE,"E12.MirrorCS"),sQuery(id+"F5.wireOp",EDGE,"E13.MirrorCS")])],"isStart":false}),makeQuery(id+"F9.opExtrude","CAP_FACE",FACE,{"disambiguationData":[OSD([sQuery(id+"F5.wireOp",EDGE,"E0.rect.top"),subQ1,sQuery(id+"F5.wireOp",EDGE,"E14.MirrorCS"),sQuery(id+"F5.wireOp",EDGE,"E15.MirrorCS")])],"isStart":false}),makeQuery(id+"F9.opExtrude","CAP_FACE",FACE,{"disambiguationData":[OSD([subQ0,subQ1,sQuery(id+"F5.wireOp",EDGE,"E10.MirrorCS"),sQuery(id+"F5.wireOp",EDGE,"E11.MirrorCS")])],"isStart":false}),makeQuery(id+"F9.opExtrude","CAP_FACE",FACE,{"disambiguationData":[OSD([sQuery(id+"F5.wireOp",EDGE,"E0.rect.right"),subQ1,sQuery(id+"F5.wireOp",EDGE,"E5.3.0"),sQuery(id+"F5.wireOp",EDGE,"E5.3.1")])],"isStart":false})]})]});}
            fillet(context, id + "F12", {"entities" : qUnion([Q0, Q1, Q2, Q3, Q4, Q5, Q6, Q7, Q8, Q9, Q10, Q11, Q12, Q13]), "radius" : 2 * mm, "tangentPropagation" : true, "allowEdgeOverflow" : false});
        }
        {
            var Q0;
            {var subQ0=sQuery(id+"F5.wireOp",EDGE,"E4.0");Q0=makeQuery(id+"F9.boolean.opBoolean","SPLIT",EDGE,{"disambiguationData":[TD([makeQuery(id+"F9.opExtrude","SWEPT_FACE",FACE,{"disambiguationData":[OSD([sQuery(id+"F5.wireOp",EDGE,"E5.3.0")])]})])],"derivedFrom":makeQuery(id+"F7.opExtrude","CAP_EDGE",EDGE,{"disambiguationData":[OSD([subQ0])],"isStart":true})});}
            var Q1;
            {var subQ0=sQuery(id+"F5.wireOp",EDGE,"E4.0");Q1=makeQuery(id+"F9.boolean.opBoolean","SPLIT",EDGE,{"disambiguationData":[TD([makeQuery(id+"F9.opExtrude","SWEPT_FACE",FACE,{"disambiguationData":[OSD([sQuery(id+"F5.wireOp",EDGE,"E11.MirrorCS")])]})])],"derivedFrom":makeQuery(id+"F7.opExtrude","CAP_EDGE",EDGE,{"disambiguationData":[OSD([subQ0])],"isStart":true})});}
            var Q2;
            Q2=makeQuery(id+"F9.opExtrude","SWEPT_EDGE",EDGE,{"disambiguationData":[OSD([sQuery(id+"F5.wireOp",EDGE,"E4.0"),sQuery(id+"F5.wireOp",EDGE,"E12.MirrorCS")])]});
            var Q3;
            Q3=makeQuery(id+"F9.opExtrude","SWEPT_EDGE",EDGE,{"disambiguationData":[OSD([sQuery(id+"F5.wireOp",EDGE,"E4.0"),sQuery(id+"F5.wireOp",EDGE,"E13.MirrorCS")])]});
            var Q4;
            Q4=makeQuery(id+"F9.opExtrude","SWEPT_EDGE",EDGE,{"disambiguationData":[OSD([sQuery(id+"F5.wireOp",EDGE,"E4.0"),sQuery(id+"F5.wireOp",EDGE,"E11.MirrorCS")])]});
            var Q5;
            Q5=makeQuery(id+"F9.opExtrude","CAP_EDGE",EDGE,{"disambiguationData":[OSD([sQuery(id+"F5.wireOp",EDGE,"E11.MirrorCS")])],"isStart":true});
            var Q6;
            Q6=makeQuery(id+"F9.opExtrude","CAP_EDGE",EDGE,{"disambiguationData":[OSD([sQuery(id+"F5.wireOp",EDGE,"E13.MirrorCS")])],"isStart":true});
            var Q7;
            Q7=makeQuery(id+"F9.opExtrude","CAP_EDGE",EDGE,{"disambiguationData":[OSD([sQuery(id+"F5.wireOp",EDGE,"E12.MirrorCS")])],"isStart":true});
            var Q8;
            Q8=makeQuery(id+"F9.opExtrude","CAP_EDGE",EDGE,{"disambiguationData":[OSD([sQuery(id+"F5.wireOp",EDGE,"E5.3.0")])],"isStart":true});
            var Q9;
            Q9=makeQuery(id+"F9.opExtrude","CAP_EDGE",EDGE,{"disambiguationData":[OSD([sQuery(id+"F5.wireOp",EDGE,"E5.3.1")])],"isStart":true});
            var Q10;
            {var subQ0=sQuery(id+"F5.wireOp",EDGE,"E4.0");Q10=makeQuery(id+"F9.boolean.opBoolean","SPLIT",EDGE,{"disambiguationData":[TD([makeQuery(id+"F9.opExtrude","SWEPT_FACE",FACE,{"disambiguationData":[OSD([sQuery(id+"F5.wireOp",EDGE,"E5.3.1")])]})])],"derivedFrom":makeQuery(id+"F7.opExtrude","CAP_EDGE",EDGE,{"disambiguationData":[OSD([subQ0])],"isStart":true})});}
            var Q11;
            Q11=makeQuery(id+"F9.opExtrude","CAP_EDGE",EDGE,{"disambiguationData":[OSD([sQuery(id+"F5.wireOp",EDGE,"E14.MirrorCS")])],"isStart":true});
            var Q12;
            Q12=makeQuery(id+"F9.opExtrude","CAP_EDGE",EDGE,{"disambiguationData":[OSD([sQuery(id+"F5.wireOp",EDGE,"E15.MirrorCS")])],"isStart":true});
            var Q13;
            Q13=makeQuery(id+"F9.opExtrude","CAP_EDGE",EDGE,{"disambiguationData":[OSD([sQuery(id+"F5.wireOp",EDGE,"E10.MirrorCS")])],"isStart":true});
            var Q14;
            Q14=makeQuery(id+"F9.opExtrude","SWEPT_EDGE",EDGE,{"disambiguationData":[OSD([sQuery(id+"F5.wireOp",EDGE,"E4.0"),sQuery(id+"F5.wireOp",EDGE,"E14.MirrorCS")])]});
            var Q15;
            Q15=makeQuery(id+"F9.opExtrude","SWEPT_EDGE",EDGE,{"disambiguationData":[OSD([sQuery(id+"F5.wireOp",EDGE,"E4.0"),sQuery(id+"F5.wireOp",EDGE,"E15.MirrorCS")])]});
            var Q16;
            Q16=makeQuery(id+"F9.opExtrude","SWEPT_EDGE",EDGE,{"disambiguationData":[OSD([sQuery(id+"F5.wireOp",EDGE,"E4.0"),sQuery(id+"F5.wireOp",EDGE,"E5.3.1")])]});
            var Q17;
            Q17=makeQuery(id+"F9.opExtrude","SWEPT_EDGE",EDGE,{"disambiguationData":[OSD([sQuery(id+"F5.wireOp",EDGE,"E4.0"),sQuery(id+"F5.wireOp",EDGE,"E5.3.0")])]});
            var Q18;
            Q18=makeQuery(id+"F9.opExtrude","SWEPT_EDGE",EDGE,{"disambiguationData":[OSD([sQuery(id+"F5.wireOp",EDGE,"E4.0"),sQuery(id+"F5.wireOp",EDGE,"E10.MirrorCS")])]});
            var Q19;
            {var subQ0=sQuery(id+"F5.wireOp",EDGE,"E4.0");Q19=makeQuery(id+"F9.boolean.opBoolean","SPLIT",EDGE,{"disambiguationData":[TD([makeQuery(id+"F9.opExtrude","SWEPT_FACE",FACE,{"disambiguationData":[OSD([sQuery(id+"F5.wireOp",EDGE,"E10.MirrorCS")])]})])],"derivedFrom":makeQuery(id+"F7.opExtrude","CAP_EDGE",EDGE,{"disambiguationData":[OSD([subQ0])],"isStart":true})});}
            fillet(context, id + "F13", {"entities" : qUnion([Q0, Q1, Q2, Q3, Q4, Q5, Q6, Q7, Q8, Q9, Q10, Q11, Q12, Q13, Q14, Q15, Q16, Q17, Q18, Q19]), "radius" : 1.5 * mm, "tangentPropagation" : true, "allowEdgeOverflow" : false});
        }
    });
